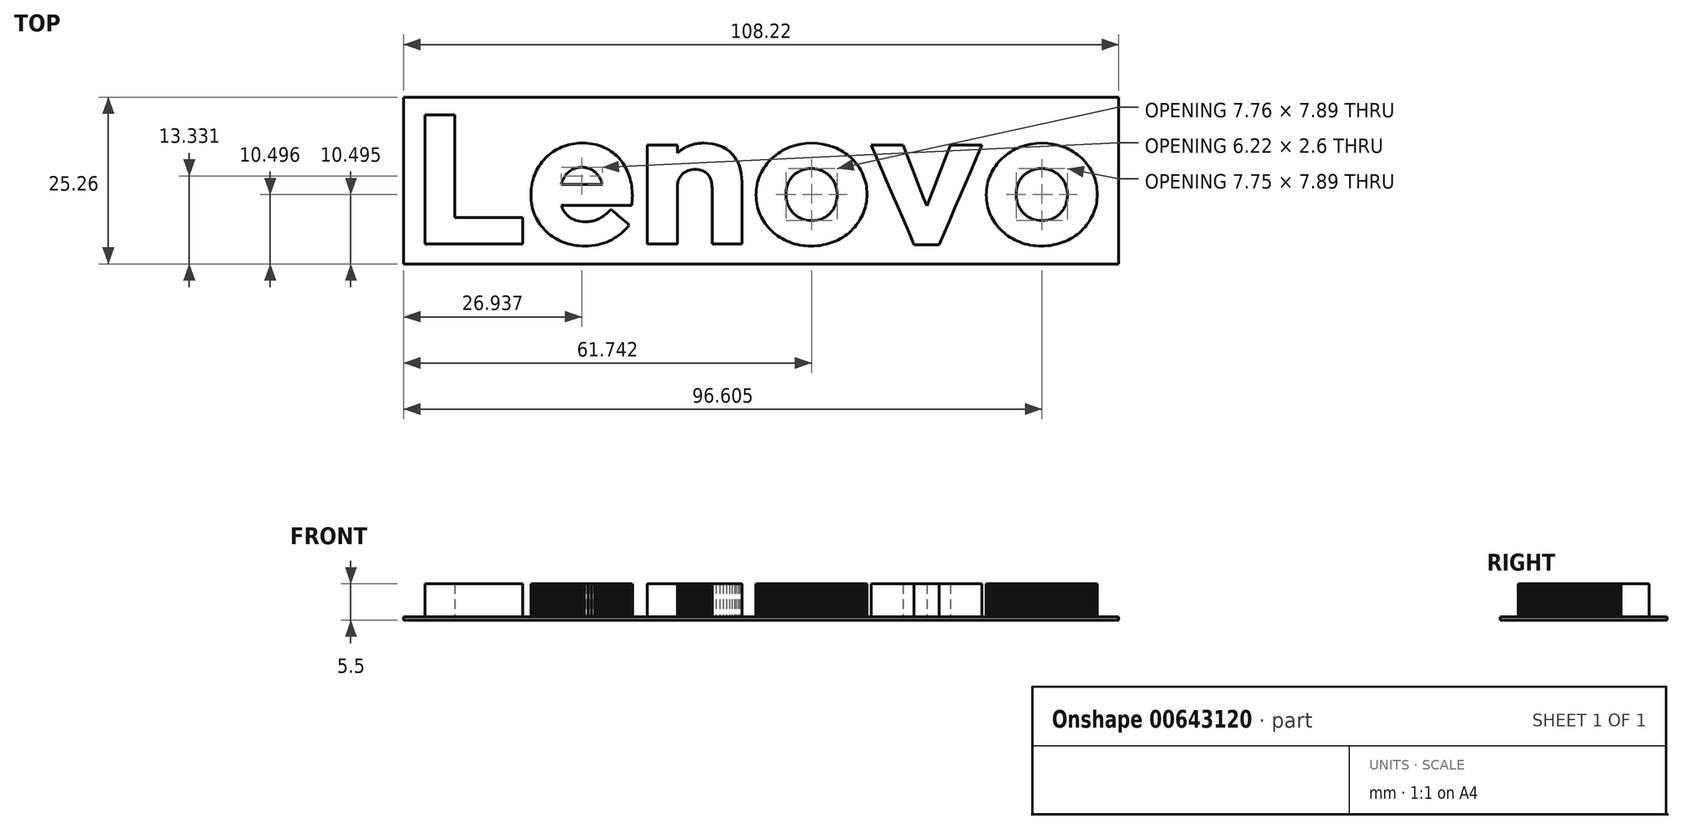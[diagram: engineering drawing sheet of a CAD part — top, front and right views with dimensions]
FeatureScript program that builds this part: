
annotation { "Feature Type Name" : "Feature", "Feature Type Description" : "" }
export const myFeature = defineFeature(function(context is Context, id is Id, definition is map)
    precondition{}
    {
        {
            var Q0;
            Q0=qCreatedBy(makeId("Top.planeOp"),FACE);
            var sketch = newSketch(context, id + "F0", { "sketchPlane" : qUnion([Q0])});
            skLineSegment(sketch, "E0", {"start": v(-46.38, -5.6) * mm, "end": v(-46.38, -3.67) * mm});
            skLineSegment(sketch, "E1", {"start": v(-46.38, -3.67) * mm, "end": v(-46.38, -1.73) * mm});
            skLineSegment(sketch, "E2", {"start": v(-46.38, -1.73) * mm, "end": v(-46.38, 0.22) * mm});
            skLineSegment(sketch, "E3", {"start": v(-46.38, 0.22) * mm, "end": v(-46.38, 2.16) * mm});
            skLineSegment(sketch, "E4", {"start": v(-46.38, 2.16) * mm, "end": v(-46.38, 4.1) * mm});
            skLineSegment(sketch, "E5", {"start": v(-46.38, 4.1) * mm, "end": v(-46.38, 6.04) * mm});
            skLineSegment(sketch, "E6", {"start": v(-46.38, 6.04) * mm, "end": v(-46.38, 7.98) * mm});
            skLineSegment(sketch, "E7", {"start": v(-46.38, 7.98) * mm, "end": v(-46.38, 9.92) * mm});
            skLineSegment(sketch, "E8", {"start": v(-46.38, 9.92) * mm, "end": v(-46.94, 9.92) * mm});
            skLineSegment(sketch, "E9", {"start": v(-46.94, 9.92) * mm, "end": v(-47.5, 9.92) * mm});
            skLineSegment(sketch, "E10", {"start": v(-47.5, 9.92) * mm, "end": v(-48.07, 9.92) * mm});
            skLineSegment(sketch, "E11", {"start": v(-48.07, 9.92) * mm, "end": v(-48.63, 9.92) * mm});
            skLineSegment(sketch, "E12", {"start": v(-48.63, 9.92) * mm, "end": v(-49.2, 9.92) * mm});
            skLineSegment(sketch, "E13", {"start": v(-49.2, 9.92) * mm, "end": v(-49.76, 9.92) * mm});
            skLineSegment(sketch, "E14", {"start": v(-49.76, 9.92) * mm, "end": v(-50.33, 9.92) * mm});
            skLineSegment(sketch, "E15", {"start": v(-50.33, 9.92) * mm, "end": v(-50.9, 9.92) * mm});
            skLineSegment(sketch, "E16", {"start": v(-50.9, 9.92) * mm, "end": v(-50.9, 7.48) * mm});
            skLineSegment(sketch, "E17", {"start": v(-50.9, 7.48) * mm, "end": v(-50.9, 5.04) * mm});
            skLineSegment(sketch, "E18", {"start": v(-50.9, 5.04) * mm, "end": v(-50.9, 2.6) * mm});
            skLineSegment(sketch, "E19", {"start": v(-50.9, 2.6) * mm, "end": v(-50.9, 0.16) * mm});
            skLineSegment(sketch, "E20", {"start": v(-50.9, 0.16) * mm, "end": v(-50.9, -2.28) * mm});
            skLineSegment(sketch, "E21", {"start": v(-50.9, -2.28) * mm, "end": v(-50.9, -4.72) * mm});
            skLineSegment(sketch, "E22", {"start": v(-50.9, -4.72) * mm, "end": v(-50.9, -7.16) * mm});
            skLineSegment(sketch, "E23", {"start": v(-50.9, -7.16) * mm, "end": v(-50.9, -9.6) * mm});
            skLineSegment(sketch, "E24", {"start": v(-50.9, -9.6) * mm, "end": v(-49.05, -9.6) * mm});
            skLineSegment(sketch, "E25", {"start": v(-49.05, -9.6) * mm, "end": v(-47.2, -9.6) * mm});
            skLineSegment(sketch, "E26", {"start": v(-47.2, -9.6) * mm, "end": v(-45.35, -9.6) * mm});
            skLineSegment(sketch, "E27", {"start": v(-45.35, -9.6) * mm, "end": v(-43.5, -9.6) * mm});
            skLineSegment(sketch, "E28", {"start": v(-43.5, -9.6) * mm, "end": v(-41.66, -9.6) * mm});
            skLineSegment(sketch, "E29", {"start": v(-41.66, -9.6) * mm, "end": v(-39.82, -9.6) * mm});
            skLineSegment(sketch, "E30", {"start": v(-39.82, -9.6) * mm, "end": v(-37.97, -9.6) * mm});
            skLineSegment(sketch, "E31", {"start": v(-37.97, -9.6) * mm, "end": v(-36.12, -9.6) * mm});
            skLineSegment(sketch, "E32", {"start": v(-36.12, -9.6) * mm, "end": v(-36.12, -9.1) * mm});
            skLineSegment(sketch, "E33", {"start": v(-36.12, -9.1) * mm, "end": v(-36.12, -8.6) * mm});
            skLineSegment(sketch, "E34", {"start": v(-36.12, -8.6) * mm, "end": v(-36.12, -8.1) * mm});
            skLineSegment(sketch, "E35", {"start": v(-36.12, -8.1) * mm, "end": v(-36.12, -7.6) * mm});
            skLineSegment(sketch, "E36", {"start": v(-36.12, -7.6) * mm, "end": v(-36.12, -7.1) * mm});
            skLineSegment(sketch, "E37", {"start": v(-36.12, -7.1) * mm, "end": v(-36.12, -6.6) * mm});
            skLineSegment(sketch, "E38", {"start": v(-36.12, -6.6) * mm, "end": v(-36.12, -6.1) * mm});
            skLineSegment(sketch, "E39", {"start": v(-36.12, -6.1) * mm, "end": v(-36.12, -5.6) * mm});
            skLineSegment(sketch, "E40", {"start": v(-36.12, -5.6) * mm, "end": v(-37.4, -5.6) * mm});
            skLineSegment(sketch, "E41", {"start": v(-37.4, -5.6) * mm, "end": v(-38.69, -5.6) * mm});
            skLineSegment(sketch, "E42", {"start": v(-38.69, -5.6) * mm, "end": v(-39.97, -5.6) * mm});
            skLineSegment(sketch, "E43", {"start": v(-39.97, -5.6) * mm, "end": v(-41.25, -5.6) * mm});
            skLineSegment(sketch, "E44", {"start": v(-41.25, -5.6) * mm, "end": v(-42.53, -5.6) * mm});
            skLineSegment(sketch, "E45", {"start": v(-42.53, -5.6) * mm, "end": v(-43.81, -5.6) * mm});
            skLineSegment(sketch, "E46", {"start": v(-43.81, -5.6) * mm, "end": v(-45.1, -5.6) * mm});
            skLineSegment(sketch, "E47", {"start": v(-45.1, -5.6) * mm, "end": v(-46.38, -5.6) * mm});
            skLineSegment(sketch, "E48", {"start": v(-24.07, -0.6) * mm, "end": v(-24.84, -0.6) * mm});
            skLineSegment(sketch, "E49", {"start": v(-24.84, -0.6) * mm, "end": v(-25.62, -0.6) * mm});
            skLineSegment(sketch, "E50", {"start": v(-25.62, -0.6) * mm, "end": v(-26.4, -0.6) * mm});
            skLineSegment(sketch, "E51", {"start": v(-26.4, -0.6) * mm, "end": v(-27.17, -0.6) * mm});
            skLineSegment(sketch, "E52", {"start": v(-27.17, -0.6) * mm, "end": v(-27.95, -0.6) * mm});
            skLineSegment(sketch, "E53", {"start": v(-27.95, -0.6) * mm, "end": v(-28.73, -0.6) * mm});
            skLineSegment(sketch, "E54", {"start": v(-28.73, -0.6) * mm, "end": v(-29.5, -0.6) * mm});
            skLineSegment(sketch, "E55", {"start": v(-29.5, -0.6) * mm, "end": v(-30.28, -0.6) * mm});
            skLineSegment(sketch, "E56", {"start": v(-30.28, -0.6) * mm, "end": v(-30.2, -0.34) * mm});
            skLineSegment(sketch, "E57", {"start": v(-30.2, -0.34) * mm, "end": v(-30.12, -0.1) * mm});
            skLineSegment(sketch, "E58", {"start": v(-30.12, -0.1) * mm, "end": v(-30.02, 0.14) * mm});
            skLineSegment(sketch, "E59", {"start": v(-30.02, 0.14) * mm, "end": v(-29.9, 0.36) * mm});
            skLineSegment(sketch, "E60", {"start": v(-29.9, 0.36) * mm, "end": v(-29.77, 0.58) * mm});
            skLineSegment(sketch, "E61", {"start": v(-29.77, 0.58) * mm, "end": v(-29.63, 0.78) * mm});
            skLineSegment(sketch, "E62", {"start": v(-29.63, 0.78) * mm, "end": v(-29.48, 0.97) * mm});
            skLineSegment(sketch, "E63", {"start": v(-29.48, 0.97) * mm, "end": v(-29.3, 1.15) * mm});
            skLineSegment(sketch, "E64", {"start": v(-29.3, 1.15) * mm, "end": v(-29.09, 1.35) * mm});
            skLineSegment(sketch, "E65", {"start": v(-29.09, 1.35) * mm, "end": v(-28.85, 1.52) * mm});
            skLineSegment(sketch, "E66", {"start": v(-28.85, 1.52) * mm, "end": v(-28.6, 1.67) * mm});
            skLineSegment(sketch, "E67", {"start": v(-28.6, 1.67) * mm, "end": v(-28.34, 1.79) * mm});
            skLineSegment(sketch, "E68", {"start": v(-28.34, 1.79) * mm, "end": v(-28.07, 1.88) * mm});
            skLineSegment(sketch, "E69", {"start": v(-28.07, 1.88) * mm, "end": v(-27.77, 1.95) * mm});
            skLineSegment(sketch, "E70", {"start": v(-27.77, 1.95) * mm, "end": v(-27.47, 1.99) * mm});
            skLineSegment(sketch, "E71", {"start": v(-27.47, 1.99) * mm, "end": v(-27.15, 2) * mm});
            skLineSegment(sketch, "E72", {"start": v(-27.15, 2) * mm, "end": v(-26.97, 2) * mm});
            skLineSegment(sketch, "E73", {"start": v(-26.97, 2) * mm, "end": v(-26.8, 1.98) * mm});
            skLineSegment(sketch, "E74", {"start": v(-26.8, 1.98) * mm, "end": v(-26.63, 1.96) * mm});
            skLineSegment(sketch, "E75", {"start": v(-26.63, 1.96) * mm, "end": v(-26.47, 1.94) * mm});
            skLineSegment(sketch, "E76", {"start": v(-26.47, 1.94) * mm, "end": v(-26.32, 1.9) * mm});
            skLineSegment(sketch, "E77", {"start": v(-26.32, 1.9) * mm, "end": v(-26.17, 1.86) * mm});
            skLineSegment(sketch, "E78", {"start": v(-26.17, 1.86) * mm, "end": v(-26.02, 1.81) * mm});
            skLineSegment(sketch, "E79", {"start": v(-26.02, 1.81) * mm, "end": v(-25.88, 1.76) * mm});
            skLineSegment(sketch, "E80", {"start": v(-25.88, 1.76) * mm, "end": v(-25.75, 1.7) * mm});
            skLineSegment(sketch, "E81", {"start": v(-25.75, 1.7) * mm, "end": v(-25.62, 1.63) * mm});
            skLineSegment(sketch, "E82", {"start": v(-25.62, 1.63) * mm, "end": v(-25.5, 1.55) * mm});
            skLineSegment(sketch, "E83", {"start": v(-25.5, 1.55) * mm, "end": v(-25.37, 1.47) * mm});
            skLineSegment(sketch, "E84", {"start": v(-25.37, 1.47) * mm, "end": v(-25.26, 1.39) * mm});
            skLineSegment(sketch, "E85", {"start": v(-25.26, 1.39) * mm, "end": v(-25.15, 1.3) * mm});
            skLineSegment(sketch, "E86", {"start": v(-25.15, 1.3) * mm, "end": v(-25.04, 1.2) * mm});
            skLineSegment(sketch, "E87", {"start": v(-25.04, 1.2) * mm, "end": v(-24.94, 1.1) * mm});
            skLineSegment(sketch, "E88", {"start": v(-24.94, 1.1) * mm, "end": v(-24.84, 1) * mm});
            skLineSegment(sketch, "E89", {"start": v(-24.84, 1) * mm, "end": v(-24.75, 0.89) * mm});
            skLineSegment(sketch, "E90", {"start": v(-24.75, 0.89) * mm, "end": v(-24.66, 0.77) * mm});
            skLineSegment(sketch, "E91", {"start": v(-24.66, 0.77) * mm, "end": v(-24.57, 0.65) * mm});
            skLineSegment(sketch, "E92", {"start": v(-24.57, 0.65) * mm, "end": v(-24.5, 0.52) * mm});
            skLineSegment(sketch, "E93", {"start": v(-24.5, 0.52) * mm, "end": v(-24.42, 0.39) * mm});
            skLineSegment(sketch, "E94", {"start": v(-24.42, 0.39) * mm, "end": v(-24.36, 0.25) * mm});
            skLineSegment(sketch, "E95", {"start": v(-24.36, 0.25) * mm, "end": v(-24.3, 0.1) * mm});
            skLineSegment(sketch, "E96", {"start": v(-24.3, 0.1) * mm, "end": v(-24.26, 0.02) * mm});
            skLineSegment(sketch, "E97", {"start": v(-24.26, 0.02) * mm, "end": v(-24.22, -0.06) * mm});
            skLineSegment(sketch, "E98", {"start": v(-24.22, -0.06) * mm, "end": v(-24.2, -0.15) * mm});
            skLineSegment(sketch, "E99", {"start": v(-24.2, -0.15) * mm, "end": v(-24.16, -0.24) * mm});
            skLineSegment(sketch, "E100", {"start": v(-24.16, -0.24) * mm, "end": v(-24.14, -0.33) * mm});
            skLineSegment(sketch, "E101", {"start": v(-24.14, -0.33) * mm, "end": v(-24.11, -0.42) * mm});
            skLineSegment(sketch, "E102", {"start": v(-24.11, -0.42) * mm, "end": v(-24.09, -0.5) * mm});
            skLineSegment(sketch, "E103", {"start": v(-24.09, -0.5) * mm, "end": v(-24.07, -0.6) * mm});
            skLineSegment(sketch, "E104", {"start": v(-19.97, 0.67) * mm, "end": v(-20.1, 1.03) * mm});
            skLineSegment(sketch, "E105", {"start": v(-20.1, 1.03) * mm, "end": v(-20.24, 1.38) * mm});
            skLineSegment(sketch, "E106", {"start": v(-20.24, 1.38) * mm, "end": v(-20.4, 1.71) * mm});
            skLineSegment(sketch, "E107", {"start": v(-20.4, 1.71) * mm, "end": v(-20.57, 2.04) * mm});
            skLineSegment(sketch, "E108", {"start": v(-20.57, 2.04) * mm, "end": v(-20.75, 2.36) * mm});
            skLineSegment(sketch, "E109", {"start": v(-20.75, 2.36) * mm, "end": v(-20.95, 2.66) * mm});
            skLineSegment(sketch, "E110", {"start": v(-20.95, 2.66) * mm, "end": v(-21.16, 2.96) * mm});
            skLineSegment(sketch, "E111", {"start": v(-21.16, 2.96) * mm, "end": v(-21.4, 3.24) * mm});
            skLineSegment(sketch, "E112", {"start": v(-21.4, 3.24) * mm, "end": v(-21.64, 3.51) * mm});
            skLineSegment(sketch, "E113", {"start": v(-21.64, 3.51) * mm, "end": v(-21.9, 3.77) * mm});
            skLineSegment(sketch, "E114", {"start": v(-21.9, 3.77) * mm, "end": v(-22.18, 4.01) * mm});
            skLineSegment(sketch, "E115", {"start": v(-22.18, 4.01) * mm, "end": v(-22.47, 4.24) * mm});
            skLineSegment(sketch, "E116", {"start": v(-22.47, 4.24) * mm, "end": v(-22.78, 4.46) * mm});
            skLineSegment(sketch, "E117", {"start": v(-22.78, 4.46) * mm, "end": v(-23.1, 4.66) * mm});
            skLineSegment(sketch, "E118", {"start": v(-23.1, 4.66) * mm, "end": v(-23.44, 4.84) * mm});
            skLineSegment(sketch, "E119", {"start": v(-23.44, 4.84) * mm, "end": v(-23.79, 5.02) * mm});
            skLineSegment(sketch, "E120", {"start": v(-23.79, 5.02) * mm, "end": v(-24.15, 5.17) * mm});
            skLineSegment(sketch, "E121", {"start": v(-24.15, 5.17) * mm, "end": v(-24.53, 5.3) * mm});
            skLineSegment(sketch, "E122", {"start": v(-24.53, 5.3) * mm, "end": v(-24.93, 5.42) * mm});
            skLineSegment(sketch, "E123", {"start": v(-24.93, 5.42) * mm, "end": v(-25.34, 5.51) * mm});
            skLineSegment(sketch, "E124", {"start": v(-25.34, 5.51) * mm, "end": v(-25.76, 5.58) * mm});
            skLineSegment(sketch, "E125", {"start": v(-25.76, 5.58) * mm, "end": v(-26.2, 5.63) * mm});
            skLineSegment(sketch, "E126", {"start": v(-26.2, 5.63) * mm, "end": v(-26.65, 5.67) * mm});
            skLineSegment(sketch, "E127", {"start": v(-26.65, 5.67) * mm, "end": v(-27.1, 5.68) * mm});
            skLineSegment(sketch, "E128", {"start": v(-27.1, 5.68) * mm, "end": v(-27.53, 5.67) * mm});
            skLineSegment(sketch, "E129", {"start": v(-27.53, 5.67) * mm, "end": v(-27.95, 5.64) * mm});
            skLineSegment(sketch, "E130", {"start": v(-27.95, 5.64) * mm, "end": v(-28.35, 5.59) * mm});
            skLineSegment(sketch, "E131", {"start": v(-28.35, 5.59) * mm, "end": v(-28.75, 5.52) * mm});
            skLineSegment(sketch, "E132", {"start": v(-28.75, 5.52) * mm, "end": v(-29.14, 5.43) * mm});
            skLineSegment(sketch, "E133", {"start": v(-29.14, 5.43) * mm, "end": v(-29.51, 5.33) * mm});
            skLineSegment(sketch, "E134", {"start": v(-29.51, 5.33) * mm, "end": v(-29.88, 5.2) * mm});
            skLineSegment(sketch, "E135", {"start": v(-29.88, 5.2) * mm, "end": v(-30.24, 5.06) * mm});
            skLineSegment(sketch, "E136", {"start": v(-30.24, 5.06) * mm, "end": v(-30.59, 4.9) * mm});
            skLineSegment(sketch, "E137", {"start": v(-30.59, 4.9) * mm, "end": v(-30.92, 4.73) * mm});
            skLineSegment(sketch, "E138", {"start": v(-30.92, 4.73) * mm, "end": v(-31.25, 4.54) * mm});
            skLineSegment(sketch, "E139", {"start": v(-31.25, 4.54) * mm, "end": v(-31.56, 4.33) * mm});
            skLineSegment(sketch, "E140", {"start": v(-31.56, 4.33) * mm, "end": v(-31.86, 4.12) * mm});
            skLineSegment(sketch, "E141", {"start": v(-31.86, 4.12) * mm, "end": v(-32.15, 3.89) * mm});
            skLineSegment(sketch, "E142", {"start": v(-32.15, 3.89) * mm, "end": v(-32.43, 3.64) * mm});
            skLineSegment(sketch, "E143", {"start": v(-32.43, 3.64) * mm, "end": v(-32.7, 3.38) * mm});
            skLineSegment(sketch, "E144", {"start": v(-32.7, 3.38) * mm, "end": v(-32.94, 3.11) * mm});
            skLineSegment(sketch, "E145", {"start": v(-32.94, 3.11) * mm, "end": v(-33.18, 2.83) * mm});
            skLineSegment(sketch, "E146", {"start": v(-33.18, 2.83) * mm, "end": v(-33.4, 2.53) * mm});
            skLineSegment(sketch, "E147", {"start": v(-33.4, 2.53) * mm, "end": v(-33.61, 2.23) * mm});
            skLineSegment(sketch, "E148", {"start": v(-33.61, 2.23) * mm, "end": v(-33.8, 1.91) * mm});
            skLineSegment(sketch, "E149", {"start": v(-33.8, 1.91) * mm, "end": v(-33.98, 1.59) * mm});
            skLineSegment(sketch, "E150", {"start": v(-33.98, 1.59) * mm, "end": v(-34.14, 1.25) * mm});
            skLineSegment(sketch, "E151", {"start": v(-34.14, 1.25) * mm, "end": v(-34.3, 0.9) * mm});
            skLineSegment(sketch, "E152", {"start": v(-34.3, 0.9) * mm, "end": v(-34.42, 0.55) * mm});
            skLineSegment(sketch, "E153", {"start": v(-34.42, 0.55) * mm, "end": v(-34.54, 0.19) * mm});
            skLineSegment(sketch, "E154", {"start": v(-34.54, 0.19) * mm, "end": v(-34.64, -0.18) * mm});
            skLineSegment(sketch, "E155", {"start": v(-34.64, -0.18) * mm, "end": v(-34.72, -0.56) * mm});
            skLineSegment(sketch, "E156", {"start": v(-34.72, -0.56) * mm, "end": v(-34.78, -0.95) * mm});
            skLineSegment(sketch, "E157", {"start": v(-34.78, -0.95) * mm, "end": v(-34.82, -1.34) * mm});
            skLineSegment(sketch, "E158", {"start": v(-34.82, -1.34) * mm, "end": v(-34.85, -1.75) * mm});
            skLineSegment(sketch, "E159", {"start": v(-34.85, -1.75) * mm, "end": v(-34.86, -2.16) * mm});
            skLineSegment(sketch, "E160", {"start": v(-34.86, -2.16) * mm, "end": v(-34.85, -2.59) * mm});
            skLineSegment(sketch, "E161", {"start": v(-34.85, -2.59) * mm, "end": v(-34.82, -3) * mm});
            skLineSegment(sketch, "E162", {"start": v(-34.82, -3) * mm, "end": v(-34.77, -3.4) * mm});
            skLineSegment(sketch, "E163", {"start": v(-34.77, -3.4) * mm, "end": v(-34.7, -3.8) * mm});
            skLineSegment(sketch, "E164", {"start": v(-34.7, -3.8) * mm, "end": v(-34.61, -4.2) * mm});
            skLineSegment(sketch, "E165", {"start": v(-34.61, -4.2) * mm, "end": v(-34.5, -4.57) * mm});
            skLineSegment(sketch, "E166", {"start": v(-34.5, -4.57) * mm, "end": v(-34.38, -4.95) * mm});
            skLineSegment(sketch, "E167", {"start": v(-34.38, -4.95) * mm, "end": v(-34.24, -5.3) * mm});
            skLineSegment(sketch, "E168", {"start": v(-34.24, -5.3) * mm, "end": v(-34.07, -5.66) * mm});
            skLineSegment(sketch, "E169", {"start": v(-34.07, -5.66) * mm, "end": v(-33.89, -6) * mm});
            skLineSegment(sketch, "E170", {"start": v(-33.89, -6) * mm, "end": v(-33.7, -6.32) * mm});
            skLineSegment(sketch, "E171", {"start": v(-33.7, -6.32) * mm, "end": v(-33.48, -6.64) * mm});
            skLineSegment(sketch, "E172", {"start": v(-33.48, -6.64) * mm, "end": v(-33.26, -6.94) * mm});
            skLineSegment(sketch, "E173", {"start": v(-33.26, -6.94) * mm, "end": v(-33.02, -7.22) * mm});
            skLineSegment(sketch, "E174", {"start": v(-33.02, -7.22) * mm, "end": v(-32.77, -7.5) * mm});
            skLineSegment(sketch, "E175", {"start": v(-32.77, -7.5) * mm, "end": v(-32.5, -7.76) * mm});
            skLineSegment(sketch, "E176", {"start": v(-32.5, -7.76) * mm, "end": v(-32.22, -8) * mm});
            skLineSegment(sketch, "E177", {"start": v(-32.22, -8) * mm, "end": v(-31.93, -8.24) * mm});
            skLineSegment(sketch, "E178", {"start": v(-31.93, -8.24) * mm, "end": v(-31.63, -8.46) * mm});
            skLineSegment(sketch, "E179", {"start": v(-31.63, -8.46) * mm, "end": v(-31.31, -8.67) * mm});
            skLineSegment(sketch, "E180", {"start": v(-31.31, -8.67) * mm, "end": v(-30.98, -8.86) * mm});
            skLineSegment(sketch, "E181", {"start": v(-30.98, -8.86) * mm, "end": v(-30.64, -9.04) * mm});
            skLineSegment(sketch, "E182", {"start": v(-30.64, -9.04) * mm, "end": v(-30.29, -9.2) * mm});
            skLineSegment(sketch, "E183", {"start": v(-30.29, -9.2) * mm, "end": v(-29.93, -9.35) * mm});
            skLineSegment(sketch, "E184", {"start": v(-29.93, -9.35) * mm, "end": v(-29.55, -9.49) * mm});
            skLineSegment(sketch, "E185", {"start": v(-29.55, -9.49) * mm, "end": v(-29.17, -9.6) * mm});
            skLineSegment(sketch, "E186", {"start": v(-29.17, -9.6) * mm, "end": v(-28.78, -9.7) * mm});
            skLineSegment(sketch, "E187", {"start": v(-28.78, -9.7) * mm, "end": v(-28.4, -9.78) * mm});
            skLineSegment(sketch, "E188", {"start": v(-28.4, -9.78) * mm, "end": v(-27.99, -9.84) * mm});
            skLineSegment(sketch, "E189", {"start": v(-27.99, -9.84) * mm, "end": v(-27.58, -9.89) * mm});
            skLineSegment(sketch, "E190", {"start": v(-27.58, -9.89) * mm, "end": v(-27.17, -9.91) * mm});
            skLineSegment(sketch, "E191", {"start": v(-27.17, -9.91) * mm, "end": v(-26.75, -9.92) * mm});
            skLineSegment(sketch, "E192", {"start": v(-26.75, -9.92) * mm, "end": v(-26.22, -9.9) * mm});
            skLineSegment(sketch, "E193", {"start": v(-26.22, -9.9) * mm, "end": v(-25.7, -9.87) * mm});
            skLineSegment(sketch, "E194", {"start": v(-25.7, -9.87) * mm, "end": v(-25.2, -9.81) * mm});
            skLineSegment(sketch, "E195", {"start": v(-25.2, -9.81) * mm, "end": v(-24.73, -9.73) * mm});
            skLineSegment(sketch, "E196", {"start": v(-24.73, -9.73) * mm, "end": v(-24.26, -9.62) * mm});
            skLineSegment(sketch, "E197", {"start": v(-24.26, -9.62) * mm, "end": v(-23.82, -9.48) * mm});
            skLineSegment(sketch, "E198", {"start": v(-23.82, -9.48) * mm, "end": v(-23.4, -9.33) * mm});
            skLineSegment(sketch, "E199", {"start": v(-23.4, -9.33) * mm, "end": v(-23, -9.15) * mm});
            skLineSegment(sketch, "E200", {"start": v(-23, -9.15) * mm, "end": v(-22.61, -8.95) * mm});
            skLineSegment(sketch, "E201", {"start": v(-22.61, -8.95) * mm, "end": v(-22.24, -8.74) * mm});
            skLineSegment(sketch, "E202", {"start": v(-22.24, -8.74) * mm, "end": v(-21.89, -8.5) * mm});
            skLineSegment(sketch, "E203", {"start": v(-21.89, -8.5) * mm, "end": v(-21.54, -8.26) * mm});
            skLineSegment(sketch, "E204", {"start": v(-21.54, -8.26) * mm, "end": v(-21.21, -8) * mm});
            skLineSegment(sketch, "E205", {"start": v(-21.21, -8) * mm, "end": v(-20.9, -7.72) * mm});
            skLineSegment(sketch, "E206", {"start": v(-20.9, -7.72) * mm, "end": v(-20.6, -7.43) * mm});
            skLineSegment(sketch, "E207", {"start": v(-20.6, -7.43) * mm, "end": v(-20.3, -7.12) * mm});
            skLineSegment(sketch, "E208", {"start": v(-20.3, -7.12) * mm, "end": v(-20.26, -7.07) * mm});
            skLineSegment(sketch, "E209", {"start": v(-20.26, -7.07) * mm, "end": v(-20.21, -7.02) * mm});
            skLineSegment(sketch, "E210", {"start": v(-20.21, -7.02) * mm, "end": v(-20.17, -6.97) * mm});
            skLineSegment(sketch, "E211", {"start": v(-20.17, -6.97) * mm, "end": v(-20.12, -6.92) * mm});
            skLineSegment(sketch, "E212", {"start": v(-20.12, -6.92) * mm, "end": v(-20.08, -6.87) * mm});
            skLineSegment(sketch, "E213", {"start": v(-20.08, -6.87) * mm, "end": v(-20.04, -6.82) * mm});
            skLineSegment(sketch, "E214", {"start": v(-20.04, -6.82) * mm, "end": v(-20, -6.77) * mm});
            skLineSegment(sketch, "E215", {"start": v(-20, -6.77) * mm, "end": v(-19.95, -6.72) * mm});
            skLineSegment(sketch, "E216", {"start": v(-19.95, -6.72) * mm, "end": v(-20.3, -6.43) * mm});
            skLineSegment(sketch, "E217", {"start": v(-20.3, -6.43) * mm, "end": v(-20.64, -6.14) * mm});
            skLineSegment(sketch, "E218", {"start": v(-20.64, -6.14) * mm, "end": v(-21, -5.85) * mm});
            skLineSegment(sketch, "E219", {"start": v(-21, -5.85) * mm, "end": v(-21.34, -5.55) * mm});
            skLineSegment(sketch, "E220", {"start": v(-21.34, -5.55) * mm, "end": v(-21.69, -5.26) * mm});
            skLineSegment(sketch, "E221", {"start": v(-21.69, -5.26) * mm, "end": v(-22.04, -4.97) * mm});
            skLineSegment(sketch, "E222", {"start": v(-22.04, -4.97) * mm, "end": v(-22.38, -4.68) * mm});
            skLineSegment(sketch, "E223", {"start": v(-22.38, -4.68) * mm, "end": v(-22.73, -4.39) * mm});
            skLineSegment(sketch, "E224", {"start": v(-22.73, -4.39) * mm, "end": v(-22.78, -4.43) * mm});
            skLineSegment(sketch, "E225", {"start": v(-22.78, -4.43) * mm, "end": v(-22.82, -4.47) * mm});
            skLineSegment(sketch, "E226", {"start": v(-22.82, -4.47) * mm, "end": v(-22.87, -4.51) * mm});
            skLineSegment(sketch, "E227", {"start": v(-22.87, -4.51) * mm, "end": v(-22.92, -4.56) * mm});
            skLineSegment(sketch, "E228", {"start": v(-22.92, -4.56) * mm, "end": v(-22.96, -4.6) * mm});
            skLineSegment(sketch, "E229", {"start": v(-22.96, -4.6) * mm, "end": v(-23.01, -4.64) * mm});
            skLineSegment(sketch, "E230", {"start": v(-23.01, -4.64) * mm, "end": v(-23.06, -4.69) * mm});
            skLineSegment(sketch, "E231", {"start": v(-23.06, -4.69) * mm, "end": v(-23.1, -4.73) * mm});
            skLineSegment(sketch, "E232", {"start": v(-23.1, -4.73) * mm, "end": v(-23.3, -4.91) * mm});
            skLineSegment(sketch, "E233", {"start": v(-23.3, -4.91) * mm, "end": v(-23.52, -5.09) * mm});
            skLineSegment(sketch, "E234", {"start": v(-23.52, -5.09) * mm, "end": v(-23.72, -5.25) * mm});
            skLineSegment(sketch, "E235", {"start": v(-23.72, -5.25) * mm, "end": v(-23.93, -5.4) * mm});
            skLineSegment(sketch, "E236", {"start": v(-23.93, -5.4) * mm, "end": v(-24.14, -5.53) * mm});
            skLineSegment(sketch, "E237", {"start": v(-24.14, -5.53) * mm, "end": v(-24.35, -5.66) * mm});
            skLineSegment(sketch, "E238", {"start": v(-24.35, -5.66) * mm, "end": v(-24.55, -5.77) * mm});
            skLineSegment(sketch, "E239", {"start": v(-24.55, -5.77) * mm, "end": v(-24.76, -5.87) * mm});
            skLineSegment(sketch, "E240", {"start": v(-24.76, -5.87) * mm, "end": v(-24.97, -5.96) * mm});
            skLineSegment(sketch, "E241", {"start": v(-24.97, -5.96) * mm, "end": v(-25.18, -6.03) * mm});
            skLineSegment(sketch, "E242", {"start": v(-25.18, -6.03) * mm, "end": v(-25.41, -6.1) * mm});
            skLineSegment(sketch, "E243", {"start": v(-25.41, -6.1) * mm, "end": v(-25.65, -6.15) * mm});
            skLineSegment(sketch, "E244", {"start": v(-25.65, -6.15) * mm, "end": v(-25.9, -6.19) * mm});
            skLineSegment(sketch, "E245", {"start": v(-25.9, -6.19) * mm, "end": v(-26.15, -6.22) * mm});
            skLineSegment(sketch, "E246", {"start": v(-26.15, -6.22) * mm, "end": v(-26.42, -6.23) * mm});
            skLineSegment(sketch, "E247", {"start": v(-26.42, -6.23) * mm, "end": v(-26.69, -6.24) * mm});
            skLineSegment(sketch, "E248", {"start": v(-26.69, -6.24) * mm, "end": v(-27.04, -6.23) * mm});
            skLineSegment(sketch, "E249", {"start": v(-27.04, -6.23) * mm, "end": v(-27.39, -6.2) * mm});
            skLineSegment(sketch, "E250", {"start": v(-27.39, -6.2) * mm, "end": v(-27.71, -6.13) * mm});
            skLineSegment(sketch, "E251", {"start": v(-27.71, -6.13) * mm, "end": v(-28.02, -6.04) * mm});
            skLineSegment(sketch, "E252", {"start": v(-28.02, -6.04) * mm, "end": v(-28.32, -5.94) * mm});
            skLineSegment(sketch, "E253", {"start": v(-28.32, -5.94) * mm, "end": v(-28.6, -5.8) * mm});
            skLineSegment(sketch, "E254", {"start": v(-28.6, -5.8) * mm, "end": v(-28.87, -5.64) * mm});
            skLineSegment(sketch, "E255", {"start": v(-28.87, -5.64) * mm, "end": v(-29.13, -5.46) * mm});
            skLineSegment(sketch, "E256", {"start": v(-29.13, -5.46) * mm, "end": v(-29.32, -5.3) * mm});
            skLineSegment(sketch, "E257", {"start": v(-29.32, -5.3) * mm, "end": v(-29.5, -5.12) * mm});
            skLineSegment(sketch, "E258", {"start": v(-29.5, -5.12) * mm, "end": v(-29.65, -4.93) * mm});
            skLineSegment(sketch, "E259", {"start": v(-29.65, -4.93) * mm, "end": v(-29.8, -4.73) * mm});
            skLineSegment(sketch, "E260", {"start": v(-29.8, -4.73) * mm, "end": v(-29.93, -4.51) * mm});
            skLineSegment(sketch, "E261", {"start": v(-29.93, -4.51) * mm, "end": v(-30.04, -4.28) * mm});
            skLineSegment(sketch, "E262", {"start": v(-30.04, -4.28) * mm, "end": v(-30.15, -4.04) * mm});
            skLineSegment(sketch, "E263", {"start": v(-30.15, -4.04) * mm, "end": v(-30.23, -3.78) * mm});
            skLineSegment(sketch, "E264", {"start": v(-30.23, -3.78) * mm, "end": v(-28.9, -3.78) * mm});
            skLineSegment(sketch, "E265", {"start": v(-28.9, -3.78) * mm, "end": v(-27.58, -3.78) * mm});
            skLineSegment(sketch, "E266", {"start": v(-27.58, -3.78) * mm, "end": v(-26.25, -3.78) * mm});
            skLineSegment(sketch, "E267", {"start": v(-26.25, -3.78) * mm, "end": v(-24.93, -3.78) * mm});
            skLineSegment(sketch, "E268", {"start": v(-24.93, -3.78) * mm, "end": v(-23.6, -3.78) * mm});
            skLineSegment(sketch, "E269", {"start": v(-23.6, -3.78) * mm, "end": v(-22.27, -3.78) * mm});
            skLineSegment(sketch, "E270", {"start": v(-22.27, -3.78) * mm, "end": v(-20.94, -3.78) * mm});
            skLineSegment(sketch, "E271", {"start": v(-20.94, -3.78) * mm, "end": v(-19.62, -3.78) * mm});
            skLineSegment(sketch, "E272", {"start": v(-19.62, -3.78) * mm, "end": v(-19.61, -3.72) * mm});
            skLineSegment(sketch, "E273", {"start": v(-19.61, -3.72) * mm, "end": v(-19.6, -3.66) * mm});
            skLineSegment(sketch, "E274", {"start": v(-19.6, -3.66) * mm, "end": v(-19.6, -3.6) * mm});
            skLineSegment(sketch, "E275", {"start": v(-19.6, -3.6) * mm, "end": v(-19.59, -3.54) * mm});
            skLineSegment(sketch, "E276", {"start": v(-19.59, -3.54) * mm, "end": v(-19.58, -3.48) * mm});
            skLineSegment(sketch, "E277", {"start": v(-19.58, -3.48) * mm, "end": v(-19.58, -3.42) * mm});
            skLineSegment(sketch, "E278", {"start": v(-19.58, -3.42) * mm, "end": v(-19.57, -3.36) * mm});
            skLineSegment(sketch, "E279", {"start": v(-19.57, -3.36) * mm, "end": v(-19.56, -3.3) * mm});
            skLineSegment(sketch, "E280", {"start": v(-19.56, -3.3) * mm, "end": v(-19.55, -3.24) * mm});
            skLineSegment(sketch, "E281", {"start": v(-19.55, -3.24) * mm, "end": v(-19.55, -3.18) * mm});
            skLineSegment(sketch, "E282", {"start": v(-19.55, -3.18) * mm, "end": v(-19.54, -3.11) * mm});
            skLineSegment(sketch, "E283", {"start": v(-19.54, -3.11) * mm, "end": v(-19.53, -3.05) * mm});
            skLineSegment(sketch, "E284", {"start": v(-19.53, -3.05) * mm, "end": v(-19.53, -3) * mm});
            skLineSegment(sketch, "E285", {"start": v(-19.53, -3) * mm, "end": v(-19.52, -2.93) * mm});
            skLineSegment(sketch, "E286", {"start": v(-19.52, -2.93) * mm, "end": v(-19.52, -2.87) * mm});
            skLineSegment(sketch, "E287", {"start": v(-19.52, -2.87) * mm, "end": v(-19.52, -2.81) * mm});
            skLineSegment(sketch, "E288", {"start": v(-19.52, -2.81) * mm, "end": v(-19.51, -2.75) * mm});
            skLineSegment(sketch, "E289", {"start": v(-19.51, -2.75) * mm, "end": v(-19.51, -2.7) * mm});
            skLineSegment(sketch, "E290", {"start": v(-19.51, -2.7) * mm, "end": v(-19.5, -2.63) * mm});
            skLineSegment(sketch, "E291", {"start": v(-19.5, -2.63) * mm, "end": v(-19.5, -2.58) * mm});
            skLineSegment(sketch, "E292", {"start": v(-19.5, -2.58) * mm, "end": v(-19.5, -2.52) * mm});
            skLineSegment(sketch, "E293", {"start": v(-19.5, -2.52) * mm, "end": v(-19.5, -2.46) * mm});
            skLineSegment(sketch, "E294", {"start": v(-19.5, -2.46) * mm, "end": v(-19.5, -2.4) * mm});
            skLineSegment(sketch, "E295", {"start": v(-19.5, -2.4) * mm, "end": v(-19.5, -2.35) * mm});
            skLineSegment(sketch, "E296", {"start": v(-19.5, -2.35) * mm, "end": v(-19.5, -1.95) * mm});
            skLineSegment(sketch, "E297", {"start": v(-19.5, -1.95) * mm, "end": v(-19.53, -1.57) * mm});
            skLineSegment(sketch, "E298", {"start": v(-19.53, -1.57) * mm, "end": v(-19.57, -1.18) * mm});
            skLineSegment(sketch, "E299", {"start": v(-19.57, -1.18) * mm, "end": v(-19.62, -0.8) * mm});
            skLineSegment(sketch, "E300", {"start": v(-19.62, -0.8) * mm, "end": v(-19.69, -0.42) * mm});
            skLineSegment(sketch, "E301", {"start": v(-19.69, -0.42) * mm, "end": v(-19.77, -0.05) * mm});
            skLineSegment(sketch, "E302", {"start": v(-19.77, -0.05) * mm, "end": v(-19.86, 0.31) * mm});
            skLineSegment(sketch, "E303", {"start": v(-19.86, 0.31) * mm, "end": v(-19.97, 0.67) * mm});
            skLineSegment(sketch, "E304", {"start": v(-4.4, 4.05) * mm, "end": v(-4.8, 4.43) * mm});
            skLineSegment(sketch, "E305", {"start": v(-4.8, 4.43) * mm, "end": v(-5.25, 4.76) * mm});
            skLineSegment(sketch, "E306", {"start": v(-5.25, 4.76) * mm, "end": v(-5.73, 5.04) * mm});
            skLineSegment(sketch, "E307", {"start": v(-5.73, 5.04) * mm, "end": v(-6.25, 5.27) * mm});
            skLineSegment(sketch, "E308", {"start": v(-6.25, 5.27) * mm, "end": v(-6.8, 5.45) * mm});
            skLineSegment(sketch, "E309", {"start": v(-6.8, 5.45) * mm, "end": v(-7.4, 5.57) * mm});
            skLineSegment(sketch, "E310", {"start": v(-7.4, 5.57) * mm, "end": v(-8.02, 5.65) * mm});
            skLineSegment(sketch, "E311", {"start": v(-8.02, 5.65) * mm, "end": v(-8.69, 5.68) * mm});
            skLineSegment(sketch, "E312", {"start": v(-8.69, 5.68) * mm, "end": v(-8.92, 5.67) * mm});
            skLineSegment(sketch, "E313", {"start": v(-8.92, 5.67) * mm, "end": v(-9.15, 5.66) * mm});
            skLineSegment(sketch, "E314", {"start": v(-9.15, 5.66) * mm, "end": v(-9.37, 5.64) * mm});
            skLineSegment(sketch, "E315", {"start": v(-9.37, 5.64) * mm, "end": v(-9.59, 5.62) * mm});
            skLineSegment(sketch, "E316", {"start": v(-9.59, 5.62) * mm, "end": v(-9.8, 5.59) * mm});
            skLineSegment(sketch, "E317", {"start": v(-9.8, 5.59) * mm, "end": v(-10, 5.55) * mm});
            skLineSegment(sketch, "E318", {"start": v(-10, 5.55) * mm, "end": v(-10.2, 5.5) * mm});
            skLineSegment(sketch, "E319", {"start": v(-10.2, 5.5) * mm, "end": v(-10.4, 5.45) * mm});
            skLineSegment(sketch, "E320", {"start": v(-10.4, 5.45) * mm, "end": v(-10.58, 5.4) * mm});
            skLineSegment(sketch, "E321", {"start": v(-10.58, 5.4) * mm, "end": v(-10.76, 5.33) * mm});
            skLineSegment(sketch, "E322", {"start": v(-10.76, 5.33) * mm, "end": v(-10.94, 5.27) * mm});
            skLineSegment(sketch, "E323", {"start": v(-10.94, 5.27) * mm, "end": v(-11.12, 5.2) * mm});
            skLineSegment(sketch, "E324", {"start": v(-11.12, 5.2) * mm, "end": v(-11.3, 5.11) * mm});
            skLineSegment(sketch, "E325", {"start": v(-11.3, 5.11) * mm, "end": v(-11.46, 5.03) * mm});
            skLineSegment(sketch, "E326", {"start": v(-11.46, 5.03) * mm, "end": v(-11.63, 4.94) * mm});
            skLineSegment(sketch, "E327", {"start": v(-11.63, 4.94) * mm, "end": v(-11.79, 4.85) * mm});
            skLineSegment(sketch, "E328", {"start": v(-11.79, 4.85) * mm, "end": v(-11.91, 4.77) * mm});
            skLineSegment(sketch, "E329", {"start": v(-11.91, 4.77) * mm, "end": v(-12.03, 4.69) * mm});
            skLineSegment(sketch, "E330", {"start": v(-12.03, 4.69) * mm, "end": v(-12.15, 4.6) * mm});
            skLineSegment(sketch, "E331", {"start": v(-12.15, 4.6) * mm, "end": v(-12.27, 4.52) * mm});
            skLineSegment(sketch, "E332", {"start": v(-12.27, 4.52) * mm, "end": v(-12.38, 4.43) * mm});
            skLineSegment(sketch, "E333", {"start": v(-12.38, 4.43) * mm, "end": v(-12.5, 4.34) * mm});
            skLineSegment(sketch, "E334", {"start": v(-12.5, 4.34) * mm, "end": v(-12.6, 4.25) * mm});
            skLineSegment(sketch, "E335", {"start": v(-12.6, 4.25) * mm, "end": v(-12.7, 4.16) * mm});
            skLineSegment(sketch, "E336", {"start": v(-12.7, 4.16) * mm, "end": v(-12.7, 4.3) * mm});
            skLineSegment(sketch, "E337", {"start": v(-12.7, 4.3) * mm, "end": v(-12.7, 4.46) * mm});
            skLineSegment(sketch, "E338", {"start": v(-12.7, 4.46) * mm, "end": v(-12.7, 4.62) * mm});
            skLineSegment(sketch, "E339", {"start": v(-12.7, 4.62) * mm, "end": v(-12.7, 4.77) * mm});
            skLineSegment(sketch, "E340", {"start": v(-12.7, 4.77) * mm, "end": v(-12.7, 4.93) * mm});
            skLineSegment(sketch, "E341", {"start": v(-12.7, 4.93) * mm, "end": v(-12.7, 5.08) * mm});
            skLineSegment(sketch, "E342", {"start": v(-12.7, 5.08) * mm, "end": v(-12.7, 5.23) * mm});
            skLineSegment(sketch, "E343", {"start": v(-12.7, 5.23) * mm, "end": v(-12.7, 5.39) * mm});
            skLineSegment(sketch, "E344", {"start": v(-12.7, 5.39) * mm, "end": v(-13.27, 5.39) * mm});
            skLineSegment(sketch, "E345", {"start": v(-13.27, 5.39) * mm, "end": v(-13.84, 5.39) * mm});
            skLineSegment(sketch, "E346", {"start": v(-13.84, 5.39) * mm, "end": v(-14.4, 5.39) * mm});
            skLineSegment(sketch, "E347", {"start": v(-14.4, 5.39) * mm, "end": v(-14.97, 5.39) * mm});
            skLineSegment(sketch, "E348", {"start": v(-14.97, 5.39) * mm, "end": v(-15.53, 5.39) * mm});
            skLineSegment(sketch, "E349", {"start": v(-15.53, 5.39) * mm, "end": v(-16.1, 5.39) * mm});
            skLineSegment(sketch, "E350", {"start": v(-16.1, 5.39) * mm, "end": v(-16.67, 5.39) * mm});
            skLineSegment(sketch, "E351", {"start": v(-16.67, 5.39) * mm, "end": v(-17.23, 5.39) * mm});
            skLineSegment(sketch, "E352", {"start": v(-17.23, 5.39) * mm, "end": v(-17.23, 3.51) * mm});
            skLineSegment(sketch, "E353", {"start": v(-17.23, 3.51) * mm, "end": v(-17.23, 1.64) * mm});
            skLineSegment(sketch, "E354", {"start": v(-17.23, 1.64) * mm, "end": v(-17.23, -0.23) * mm});
            skLineSegment(sketch, "E355", {"start": v(-17.23, -0.23) * mm, "end": v(-17.23, -2.1) * mm});
            skLineSegment(sketch, "E356", {"start": v(-17.23, -2.1) * mm, "end": v(-17.23, -3.98) * mm});
            skLineSegment(sketch, "E357", {"start": v(-17.23, -3.98) * mm, "end": v(-17.23, -5.85) * mm});
            skLineSegment(sketch, "E358", {"start": v(-17.23, -5.85) * mm, "end": v(-17.23, -7.73) * mm});
            skLineSegment(sketch, "E359", {"start": v(-17.23, -7.73) * mm, "end": v(-17.23, -9.6) * mm});
            skLineSegment(sketch, "E360", {"start": v(-17.23, -9.6) * mm, "end": v(-16.67, -9.6) * mm});
            skLineSegment(sketch, "E361", {"start": v(-16.67, -9.6) * mm, "end": v(-16.1, -9.6) * mm});
            skLineSegment(sketch, "E362", {"start": v(-16.1, -9.6) * mm, "end": v(-15.53, -9.6) * mm});
            skLineSegment(sketch, "E363", {"start": v(-15.53, -9.6) * mm, "end": v(-14.97, -9.6) * mm});
            skLineSegment(sketch, "E364", {"start": v(-14.97, -9.6) * mm, "end": v(-14.4, -9.6) * mm});
            skLineSegment(sketch, "E365", {"start": v(-14.4, -9.6) * mm, "end": v(-13.84, -9.6) * mm});
            skLineSegment(sketch, "E366", {"start": v(-13.84, -9.6) * mm, "end": v(-13.27, -9.6) * mm});
            skLineSegment(sketch, "E367", {"start": v(-13.27, -9.6) * mm, "end": v(-12.7, -9.6) * mm});
            skLineSegment(sketch, "E368", {"start": v(-12.7, -9.6) * mm, "end": v(-12.7, -8.56) * mm});
            skLineSegment(sketch, "E369", {"start": v(-12.7, -8.56) * mm, "end": v(-12.7, -7.5) * mm});
            skLineSegment(sketch, "E370", {"start": v(-12.7, -7.5) * mm, "end": v(-12.7, -6.46) * mm});
            skLineSegment(sketch, "E371", {"start": v(-12.7, -6.46) * mm, "end": v(-12.7, -5.42) * mm});
            skLineSegment(sketch, "E372", {"start": v(-12.7, -5.42) * mm, "end": v(-12.7, -4.37) * mm});
            skLineSegment(sketch, "E373", {"start": v(-12.7, -4.37) * mm, "end": v(-12.7, -3.32) * mm});
            skLineSegment(sketch, "E374", {"start": v(-12.7, -3.32) * mm, "end": v(-12.7, -2.28) * mm});
            skLineSegment(sketch, "E375", {"start": v(-12.7, -2.28) * mm, "end": v(-12.7, -1.23) * mm});
            skLineSegment(sketch, "E376", {"start": v(-12.7, -1.23) * mm, "end": v(-12.7, -0.88) * mm});
            skLineSegment(sketch, "E377", {"start": v(-12.7, -0.88) * mm, "end": v(-12.66, -0.56) * mm});
            skLineSegment(sketch, "E378", {"start": v(-12.66, -0.56) * mm, "end": v(-12.6, -0.26) * mm});
            skLineSegment(sketch, "E379", {"start": v(-12.6, -0.26) * mm, "end": v(-12.52, 0.02) * mm});
            skLineSegment(sketch, "E380", {"start": v(-12.52, 0.02) * mm, "end": v(-12.41, 0.28) * mm});
            skLineSegment(sketch, "E381", {"start": v(-12.41, 0.28) * mm, "end": v(-12.28, 0.52) * mm});
            skLineSegment(sketch, "E382", {"start": v(-12.28, 0.52) * mm, "end": v(-12.13, 0.74) * mm});
            skLineSegment(sketch, "E383", {"start": v(-12.13, 0.74) * mm, "end": v(-11.95, 0.94) * mm});
            skLineSegment(sketch, "E384", {"start": v(-11.95, 0.94) * mm, "end": v(-11.76, 1.11) * mm});
            skLineSegment(sketch, "E385", {"start": v(-11.76, 1.11) * mm, "end": v(-11.55, 1.27) * mm});
            skLineSegment(sketch, "E386", {"start": v(-11.55, 1.27) * mm, "end": v(-11.33, 1.4) * mm});
            skLineSegment(sketch, "E387", {"start": v(-11.33, 1.4) * mm, "end": v(-11.09, 1.5) * mm});
            skLineSegment(sketch, "E388", {"start": v(-11.09, 1.5) * mm, "end": v(-10.84, 1.58) * mm});
            skLineSegment(sketch, "E389", {"start": v(-10.84, 1.58) * mm, "end": v(-10.57, 1.64) * mm});
            skLineSegment(sketch, "E390", {"start": v(-10.57, 1.64) * mm, "end": v(-10.28, 1.67) * mm});
            skLineSegment(sketch, "E391", {"start": v(-10.28, 1.67) * mm, "end": v(-9.98, 1.68) * mm});
            skLineSegment(sketch, "E392", {"start": v(-9.98, 1.68) * mm, "end": v(-9.68, 1.67) * mm});
            skLineSegment(sketch, "E393", {"start": v(-9.68, 1.67) * mm, "end": v(-9.4, 1.64) * mm});
            skLineSegment(sketch, "E394", {"start": v(-9.4, 1.64) * mm, "end": v(-9.14, 1.58) * mm});
            skLineSegment(sketch, "E395", {"start": v(-9.14, 1.58) * mm, "end": v(-8.9, 1.5) * mm});
            skLineSegment(sketch, "E396", {"start": v(-8.9, 1.5) * mm, "end": v(-8.67, 1.41) * mm});
            skLineSegment(sketch, "E397", {"start": v(-8.67, 1.41) * mm, "end": v(-8.46, 1.3) * mm});
            skLineSegment(sketch, "E398", {"start": v(-8.46, 1.3) * mm, "end": v(-8.27, 1.15) * mm});
            skLineSegment(sketch, "E399", {"start": v(-8.27, 1.15) * mm, "end": v(-8.1, 0.99) * mm});
            skLineSegment(sketch, "E400", {"start": v(-8.1, 0.99) * mm, "end": v(-7.94, 0.8) * mm});
            skLineSegment(sketch, "E401", {"start": v(-7.94, 0.8) * mm, "end": v(-7.8, 0.58) * mm});
            skLineSegment(sketch, "E402", {"start": v(-7.8, 0.58) * mm, "end": v(-7.7, 0.34) * mm});
            skLineSegment(sketch, "E403", {"start": v(-7.7, 0.34) * mm, "end": v(-7.6, 0.08) * mm});
            skLineSegment(sketch, "E404", {"start": v(-7.6, 0.08) * mm, "end": v(-7.52, -0.2) * mm});
            skLineSegment(sketch, "E405", {"start": v(-7.52, -0.2) * mm, "end": v(-7.47, -0.5) * mm});
            skLineSegment(sketch, "E406", {"start": v(-7.47, -0.5) * mm, "end": v(-7.44, -0.83) * mm});
            skLineSegment(sketch, "E407", {"start": v(-7.44, -0.83) * mm, "end": v(-7.43, -1.18) * mm});
            skLineSegment(sketch, "E408", {"start": v(-7.43, -1.18) * mm, "end": v(-7.43, -2.23) * mm});
            skLineSegment(sketch, "E409", {"start": v(-7.43, -2.23) * mm, "end": v(-7.43, -3.28) * mm});
            skLineSegment(sketch, "E410", {"start": v(-7.43, -3.28) * mm, "end": v(-7.43, -4.34) * mm});
            skLineSegment(sketch, "E411", {"start": v(-7.43, -4.34) * mm, "end": v(-7.43, -5.39) * mm});
            skLineSegment(sketch, "E412", {"start": v(-7.43, -5.39) * mm, "end": v(-7.43, -6.44) * mm});
            skLineSegment(sketch, "E413", {"start": v(-7.43, -6.44) * mm, "end": v(-7.43, -7.5) * mm});
            skLineSegment(sketch, "E414", {"start": v(-7.43, -7.5) * mm, "end": v(-7.43, -8.55) * mm});
            skLineSegment(sketch, "E415", {"start": v(-7.43, -8.55) * mm, "end": v(-7.43, -9.6) * mm});
            skLineSegment(sketch, "E416", {"start": v(-7.43, -9.6) * mm, "end": v(-6.86, -9.6) * mm});
            skLineSegment(sketch, "E417", {"start": v(-6.86, -9.6) * mm, "end": v(-6.3, -9.6) * mm});
            skLineSegment(sketch, "E418", {"start": v(-6.3, -9.6) * mm, "end": v(-5.73, -9.6) * mm});
            skLineSegment(sketch, "E419", {"start": v(-5.73, -9.6) * mm, "end": v(-5.17, -9.6) * mm});
            skLineSegment(sketch, "E420", {"start": v(-5.17, -9.6) * mm, "end": v(-4.6, -9.6) * mm});
            skLineSegment(sketch, "E421", {"start": v(-4.6, -9.6) * mm, "end": v(-4.04, -9.6) * mm});
            skLineSegment(sketch, "E422", {"start": v(-4.04, -9.6) * mm, "end": v(-3.47, -9.6) * mm});
            skLineSegment(sketch, "E423", {"start": v(-3.47, -9.6) * mm, "end": v(-2.9, -9.6) * mm});
            skLineSegment(sketch, "E424", {"start": v(-2.9, -9.6) * mm, "end": v(-2.9, -8.43) * mm});
            skLineSegment(sketch, "E425", {"start": v(-2.9, -8.43) * mm, "end": v(-2.9, -7.25) * mm});
            skLineSegment(sketch, "E426", {"start": v(-2.9, -7.25) * mm, "end": v(-2.9, -6.08) * mm});
            skLineSegment(sketch, "E427", {"start": v(-2.9, -6.08) * mm, "end": v(-2.9, -4.9) * mm});
            skLineSegment(sketch, "E428", {"start": v(-2.9, -4.9) * mm, "end": v(-2.9, -3.73) * mm});
            skLineSegment(sketch, "E429", {"start": v(-2.9, -3.73) * mm, "end": v(-2.9, -2.56) * mm});
            skLineSegment(sketch, "E430", {"start": v(-2.9, -2.56) * mm, "end": v(-2.9, -1.38) * mm});
            skLineSegment(sketch, "E431", {"start": v(-2.9, -1.38) * mm, "end": v(-2.9, -0.2) * mm});
            skLineSegment(sketch, "E432", {"start": v(-2.9, -0.2) * mm, "end": v(-2.93, 0.44) * mm});
            skLineSegment(sketch, "E433", {"start": v(-2.93, 0.44) * mm, "end": v(-3, 1.05) * mm});
            skLineSegment(sketch, "E434", {"start": v(-3, 1.05) * mm, "end": v(-3.12, 1.63) * mm});
            skLineSegment(sketch, "E435", {"start": v(-3.12, 1.63) * mm, "end": v(-3.28, 2.18) * mm});
            skLineSegment(sketch, "E436", {"start": v(-3.28, 2.18) * mm, "end": v(-3.5, 2.7) * mm});
            skLineSegment(sketch, "E437", {"start": v(-3.5, 2.7) * mm, "end": v(-3.75, 3.18) * mm});
            skLineSegment(sketch, "E438", {"start": v(-3.75, 3.18) * mm, "end": v(-4.06, 3.63) * mm});
            skLineSegment(sketch, "E439", {"start": v(-4.06, 3.63) * mm, "end": v(-4.4, 4.05) * mm});
            skLineSegment(sketch, "E440", {"start": v(6.1, -5.78) * mm, "end": v(5.92, -5.7) * mm});
            skLineSegment(sketch, "E441", {"start": v(5.92, -5.7) * mm, "end": v(5.75, -5.6) * mm});
            skLineSegment(sketch, "E442", {"start": v(5.75, -5.6) * mm, "end": v(5.59, -5.51) * mm});
            skLineSegment(sketch, "E443", {"start": v(5.59, -5.51) * mm, "end": v(5.43, -5.4) * mm});
            skLineSegment(sketch, "E444", {"start": v(5.43, -5.4) * mm, "end": v(5.28, -5.3) * mm});
            skLineSegment(sketch, "E445", {"start": v(5.28, -5.3) * mm, "end": v(5.13, -5.18) * mm});
            skLineSegment(sketch, "E446", {"start": v(5.13, -5.18) * mm, "end": v(5, -5.06) * mm});
            skLineSegment(sketch, "E447", {"start": v(5, -5.06) * mm, "end": v(4.86, -4.93) * mm});
            skLineSegment(sketch, "E448", {"start": v(4.86, -4.93) * mm, "end": v(4.74, -4.79) * mm});
            skLineSegment(sketch, "E449", {"start": v(4.74, -4.79) * mm, "end": v(4.62, -4.64) * mm});
            skLineSegment(sketch, "E450", {"start": v(4.62, -4.64) * mm, "end": v(4.5, -4.5) * mm});
            skLineSegment(sketch, "E451", {"start": v(4.5, -4.5) * mm, "end": v(4.4, -4.34) * mm});
            skLineSegment(sketch, "E452", {"start": v(4.4, -4.34) * mm, "end": v(4.3, -4.18) * mm});
            skLineSegment(sketch, "E453", {"start": v(4.3, -4.18) * mm, "end": v(4.2, -4.01) * mm});
            skLineSegment(sketch, "E454", {"start": v(4.2, -4.01) * mm, "end": v(4.12, -3.84) * mm});
            skLineSegment(sketch, "E455", {"start": v(4.12, -3.84) * mm, "end": v(4.05, -3.67) * mm});
            skLineSegment(sketch, "E456", {"start": v(4.05, -3.67) * mm, "end": v(3.98, -3.49) * mm});
            skLineSegment(sketch, "E457", {"start": v(3.98, -3.49) * mm, "end": v(3.92, -3.3) * mm});
            skLineSegment(sketch, "E458", {"start": v(3.92, -3.3) * mm, "end": v(3.87, -3.12) * mm});
            skLineSegment(sketch, "E459", {"start": v(3.87, -3.12) * mm, "end": v(3.83, -2.92) * mm});
            skLineSegment(sketch, "E460", {"start": v(3.83, -2.92) * mm, "end": v(3.8, -2.72) * mm});
            skLineSegment(sketch, "E461", {"start": v(3.8, -2.72) * mm, "end": v(3.77, -2.52) * mm});
            skLineSegment(sketch, "E462", {"start": v(3.77, -2.52) * mm, "end": v(3.76, -2.3) * mm});
            skLineSegment(sketch, "E463", {"start": v(3.76, -2.3) * mm, "end": v(3.75, -2.08) * mm});
            skLineSegment(sketch, "E464", {"start": v(3.75, -2.08) * mm, "end": v(3.76, -1.88) * mm});
            skLineSegment(sketch, "E465", {"start": v(3.76, -1.88) * mm, "end": v(3.77, -1.68) * mm});
            skLineSegment(sketch, "E466", {"start": v(3.77, -1.68) * mm, "end": v(3.79, -1.49) * mm});
            skLineSegment(sketch, "E467", {"start": v(3.79, -1.49) * mm, "end": v(3.82, -1.3) * mm});
            skLineSegment(sketch, "E468", {"start": v(3.82, -1.3) * mm, "end": v(3.86, -1.1) * mm});
            skLineSegment(sketch, "E469", {"start": v(3.86, -1.1) * mm, "end": v(3.9, -0.92) * mm});
            skLineSegment(sketch, "E470", {"start": v(3.9, -0.92) * mm, "end": v(3.96, -0.73) * mm});
            skLineSegment(sketch, "E471", {"start": v(3.96, -0.73) * mm, "end": v(4.02, -0.55) * mm});
            skLineSegment(sketch, "E472", {"start": v(4.02, -0.55) * mm, "end": v(4.09, -0.37) * mm});
            skLineSegment(sketch, "E473", {"start": v(4.09, -0.37) * mm, "end": v(4.17, -0.2) * mm});
            skLineSegment(sketch, "E474", {"start": v(4.17, -0.2) * mm, "end": v(4.25, -0.04) * mm});
            skLineSegment(sketch, "E475", {"start": v(4.25, -0.04) * mm, "end": v(4.35, 0.11) * mm});
            skLineSegment(sketch, "E476", {"start": v(4.35, 0.11) * mm, "end": v(4.45, 0.26) * mm});
            skLineSegment(sketch, "E477", {"start": v(4.45, 0.26) * mm, "end": v(4.56, 0.4) * mm});
            skLineSegment(sketch, "E478", {"start": v(4.56, 0.4) * mm, "end": v(4.67, 0.55) * mm});
            skLineSegment(sketch, "E479", {"start": v(4.67, 0.55) * mm, "end": v(4.8, 0.68) * mm});
            skLineSegment(sketch, "E480", {"start": v(4.8, 0.68) * mm, "end": v(4.92, 0.8) * mm});
            skLineSegment(sketch, "E481", {"start": v(4.92, 0.8) * mm, "end": v(5.06, 0.92) * mm});
            skLineSegment(sketch, "E482", {"start": v(5.06, 0.92) * mm, "end": v(5.2, 1.04) * mm});
            skLineSegment(sketch, "E483", {"start": v(5.2, 1.04) * mm, "end": v(5.35, 1.14) * mm});
            skLineSegment(sketch, "E484", {"start": v(5.35, 1.14) * mm, "end": v(5.5, 1.24) * mm});
            skLineSegment(sketch, "E485", {"start": v(5.5, 1.24) * mm, "end": v(5.67, 1.34) * mm});
            skLineSegment(sketch, "E486", {"start": v(5.67, 1.34) * mm, "end": v(5.84, 1.43) * mm});
            skLineSegment(sketch, "E487", {"start": v(5.84, 1.43) * mm, "end": v(6.01, 1.5) * mm});
            skLineSegment(sketch, "E488", {"start": v(6.01, 1.5) * mm, "end": v(6.2, 1.58) * mm});
            skLineSegment(sketch, "E489", {"start": v(6.2, 1.58) * mm, "end": v(6.37, 1.64) * mm});
            skLineSegment(sketch, "E490", {"start": v(6.37, 1.64) * mm, "end": v(6.56, 1.7) * mm});
            skLineSegment(sketch, "E491", {"start": v(6.56, 1.7) * mm, "end": v(6.76, 1.74) * mm});
            skLineSegment(sketch, "E492", {"start": v(6.76, 1.74) * mm, "end": v(6.96, 1.77) * mm});
            skLineSegment(sketch, "E493", {"start": v(6.96, 1.77) * mm, "end": v(7.16, 1.8) * mm});
            skLineSegment(sketch, "E494", {"start": v(7.16, 1.8) * mm, "end": v(7.37, 1.8) * mm});
            skLineSegment(sketch, "E495", {"start": v(7.37, 1.8) * mm, "end": v(7.59, 1.81) * mm});
            skLineSegment(sketch, "E496", {"start": v(7.59, 1.81) * mm, "end": v(7.8, 1.8) * mm});
            skLineSegment(sketch, "E497", {"start": v(7.8, 1.8) * mm, "end": v(8.01, 1.8) * mm});
            skLineSegment(sketch, "E498", {"start": v(8.01, 1.8) * mm, "end": v(8.22, 1.77) * mm});
            skLineSegment(sketch, "E499", {"start": v(8.22, 1.77) * mm, "end": v(8.42, 1.74) * mm});
            skLineSegment(sketch, "E500", {"start": v(8.42, 1.74) * mm, "end": v(8.61, 1.7) * mm});
            skLineSegment(sketch, "E501", {"start": v(8.61, 1.7) * mm, "end": v(8.8, 1.64) * mm});
            skLineSegment(sketch, "E502", {"start": v(8.8, 1.64) * mm, "end": v(8.99, 1.58) * mm});
            skLineSegment(sketch, "E503", {"start": v(8.99, 1.58) * mm, "end": v(9.16, 1.5) * mm});
            skLineSegment(sketch, "E504", {"start": v(9.16, 1.5) * mm, "end": v(9.34, 1.42) * mm});
            skLineSegment(sketch, "E505", {"start": v(9.34, 1.42) * mm, "end": v(9.5, 1.34) * mm});
            skLineSegment(sketch, "E506", {"start": v(9.5, 1.34) * mm, "end": v(9.67, 1.24) * mm});
            skLineSegment(sketch, "E507", {"start": v(9.67, 1.24) * mm, "end": v(9.83, 1.14) * mm});
            skLineSegment(sketch, "E508", {"start": v(9.83, 1.14) * mm, "end": v(9.98, 1.03) * mm});
            skLineSegment(sketch, "E509", {"start": v(9.98, 1.03) * mm, "end": v(10.13, 0.92) * mm});
            skLineSegment(sketch, "E510", {"start": v(10.13, 0.92) * mm, "end": v(10.27, 0.8) * mm});
            skLineSegment(sketch, "E511", {"start": v(10.27, 0.8) * mm, "end": v(10.4, 0.67) * mm});
            skLineSegment(sketch, "E512", {"start": v(10.4, 0.67) * mm, "end": v(10.52, 0.53) * mm});
            skLineSegment(sketch, "E513", {"start": v(10.52, 0.53) * mm, "end": v(10.64, 0.39) * mm});
            skLineSegment(sketch, "E514", {"start": v(10.64, 0.39) * mm, "end": v(10.76, 0.24) * mm});
            skLineSegment(sketch, "E515", {"start": v(10.76, 0.24) * mm, "end": v(10.86, 0.09) * mm});
            skLineSegment(sketch, "E516", {"start": v(10.86, 0.09) * mm, "end": v(10.96, -0.07) * mm});
            skLineSegment(sketch, "E517", {"start": v(10.96, -0.07) * mm, "end": v(11.05, -0.24) * mm});
            skLineSegment(sketch, "E518", {"start": v(11.05, -0.24) * mm, "end": v(11.14, -0.4) * mm});
            skLineSegment(sketch, "E519", {"start": v(11.14, -0.4) * mm, "end": v(11.21, -0.59) * mm});
            skLineSegment(sketch, "E520", {"start": v(11.21, -0.59) * mm, "end": v(11.28, -0.77) * mm});
            skLineSegment(sketch, "E521", {"start": v(11.28, -0.77) * mm, "end": v(11.34, -0.96) * mm});
            skLineSegment(sketch, "E522", {"start": v(11.34, -0.96) * mm, "end": v(11.4, -1.15) * mm});
            skLineSegment(sketch, "E523", {"start": v(11.4, -1.15) * mm, "end": v(11.44, -1.35) * mm});
            skLineSegment(sketch, "E524", {"start": v(11.44, -1.35) * mm, "end": v(11.47, -1.55) * mm});
            skLineSegment(sketch, "E525", {"start": v(11.47, -1.55) * mm, "end": v(11.5, -1.75) * mm});
            skLineSegment(sketch, "E526", {"start": v(11.5, -1.75) * mm, "end": v(11.5, -1.97) * mm});
            skLineSegment(sketch, "E527", {"start": v(11.5, -1.97) * mm, "end": v(11.51, -2.19) * mm});
            skLineSegment(sketch, "E528", {"start": v(11.51, -2.19) * mm, "end": v(11.5, -2.39) * mm});
            skLineSegment(sketch, "E529", {"start": v(11.5, -2.39) * mm, "end": v(11.5, -2.58) * mm});
            skLineSegment(sketch, "E530", {"start": v(11.5, -2.58) * mm, "end": v(11.47, -2.78) * mm});
            skLineSegment(sketch, "E531", {"start": v(11.47, -2.78) * mm, "end": v(11.44, -2.97) * mm});
            skLineSegment(sketch, "E532", {"start": v(11.44, -2.97) * mm, "end": v(11.4, -3.16) * mm});
            skLineSegment(sketch, "E533", {"start": v(11.4, -3.16) * mm, "end": v(11.36, -3.34) * mm});
            skLineSegment(sketch, "E534", {"start": v(11.36, -3.34) * mm, "end": v(11.3, -3.53) * mm});
            skLineSegment(sketch, "E535", {"start": v(11.3, -3.53) * mm, "end": v(11.23, -3.7) * mm});
            skLineSegment(sketch, "E536", {"start": v(11.23, -3.7) * mm, "end": v(11.17, -3.88) * mm});
            skLineSegment(sketch, "E537", {"start": v(11.17, -3.88) * mm, "end": v(11.09, -4.05) * mm});
            skLineSegment(sketch, "E538", {"start": v(11.09, -4.05) * mm, "end": v(11, -4.21) * mm});
            skLineSegment(sketch, "E539", {"start": v(11, -4.21) * mm, "end": v(10.91, -4.37) * mm});
            skLineSegment(sketch, "E540", {"start": v(10.91, -4.37) * mm, "end": v(10.8, -4.52) * mm});
            skLineSegment(sketch, "E541", {"start": v(10.8, -4.52) * mm, "end": v(10.7, -4.67) * mm});
            skLineSegment(sketch, "E542", {"start": v(10.7, -4.67) * mm, "end": v(10.59, -4.8) * mm});
            skLineSegment(sketch, "E543", {"start": v(10.59, -4.8) * mm, "end": v(10.47, -4.94) * mm});
            skLineSegment(sketch, "E544", {"start": v(10.47, -4.94) * mm, "end": v(10.34, -5.07) * mm});
            skLineSegment(sketch, "E545", {"start": v(10.34, -5.07) * mm, "end": v(10.2, -5.19) * mm});
            skLineSegment(sketch, "E546", {"start": v(10.2, -5.19) * mm, "end": v(10.06, -5.3) * mm});
            skLineSegment(sketch, "E547", {"start": v(10.06, -5.3) * mm, "end": v(9.9, -5.41) * mm});
            skLineSegment(sketch, "E548", {"start": v(9.9, -5.41) * mm, "end": v(9.75, -5.51) * mm});
            skLineSegment(sketch, "E549", {"start": v(9.75, -5.51) * mm, "end": v(9.59, -5.6) * mm});
            skLineSegment(sketch, "E550", {"start": v(9.59, -5.6) * mm, "end": v(9.42, -5.7) * mm});
            skLineSegment(sketch, "E551", {"start": v(9.42, -5.7) * mm, "end": v(9.25, -5.78) * mm});
            skLineSegment(sketch, "E552", {"start": v(9.25, -5.78) * mm, "end": v(8.9, -5.9) * mm});
            skLineSegment(sketch, "E553", {"start": v(8.9, -5.9) * mm, "end": v(8.5, -6) * mm});
            skLineSegment(sketch, "E554", {"start": v(8.5, -6) * mm, "end": v(8.1, -6.06) * mm});
            skLineSegment(sketch, "E555", {"start": v(8.1, -6.06) * mm, "end": v(7.7, -6.08) * mm});
            skLineSegment(sketch, "E556", {"start": v(7.7, -6.08) * mm, "end": v(7.28, -6.07) * mm});
            skLineSegment(sketch, "E557", {"start": v(7.28, -6.07) * mm, "end": v(6.87, -6) * mm});
            skLineSegment(sketch, "E558", {"start": v(6.87, -6) * mm, "end": v(6.47, -5.91) * mm});
            skLineSegment(sketch, "E559", {"start": v(6.47, -5.91) * mm, "end": v(6.1, -5.78) * mm});
            skLineSegment(sketch, "E560", {"start": v(13.65, 3.4) * mm, "end": v(13.37, 3.66) * mm});
            skLineSegment(sketch, "E561", {"start": v(13.37, 3.66) * mm, "end": v(13.07, 3.9) * mm});
            skLineSegment(sketch, "E562", {"start": v(13.07, 3.9) * mm, "end": v(12.75, 4.13) * mm});
            skLineSegment(sketch, "E563", {"start": v(12.75, 4.13) * mm, "end": v(12.43, 4.35) * mm});
            skLineSegment(sketch, "E564", {"start": v(12.43, 4.35) * mm, "end": v(12.09, 4.55) * mm});
            skLineSegment(sketch, "E565", {"start": v(12.09, 4.55) * mm, "end": v(11.74, 4.74) * mm});
            skLineSegment(sketch, "E566", {"start": v(11.74, 4.74) * mm, "end": v(11.37, 4.9) * mm});
            skLineSegment(sketch, "E567", {"start": v(11.37, 4.9) * mm, "end": v(11, 5.07) * mm});
            skLineSegment(sketch, "E568", {"start": v(11, 5.07) * mm, "end": v(10.2, 5.33) * mm});
            skLineSegment(sketch, "E569", {"start": v(10.2, 5.33) * mm, "end": v(9.37, 5.52) * mm});
            skLineSegment(sketch, "E570", {"start": v(9.37, 5.52) * mm, "end": v(8.51, 5.64) * mm});
            skLineSegment(sketch, "E571", {"start": v(8.51, 5.64) * mm, "end": v(7.64, 5.67) * mm});
            skLineSegment(sketch, "E572", {"start": v(7.64, 5.67) * mm, "end": v(6.77, 5.63) * mm});
            skLineSegment(sketch, "E573", {"start": v(6.77, 5.63) * mm, "end": v(5.91, 5.52) * mm});
            skLineSegment(sketch, "E574", {"start": v(5.91, 5.52) * mm, "end": v(5.08, 5.32) * mm});
            skLineSegment(sketch, "E575", {"start": v(5.08, 5.32) * mm, "end": v(4.3, 5.05) * mm});
            skLineSegment(sketch, "E576", {"start": v(4.3, 5.05) * mm, "end": v(3.91, 4.9) * mm});
            skLineSegment(sketch, "E577", {"start": v(3.91, 4.9) * mm, "end": v(3.55, 4.72) * mm});
            skLineSegment(sketch, "E578", {"start": v(3.55, 4.72) * mm, "end": v(3.2, 4.53) * mm});
            skLineSegment(sketch, "E579", {"start": v(3.2, 4.53) * mm, "end": v(2.86, 4.32) * mm});
            skLineSegment(sketch, "E580", {"start": v(2.86, 4.32) * mm, "end": v(2.54, 4.1) * mm});
            skLineSegment(sketch, "E581", {"start": v(2.54, 4.1) * mm, "end": v(2.22, 3.87) * mm});
            skLineSegment(sketch, "E582", {"start": v(2.22, 3.87) * mm, "end": v(1.92, 3.63) * mm});
            skLineSegment(sketch, "E583", {"start": v(1.92, 3.63) * mm, "end": v(1.63, 3.37) * mm});
            skLineSegment(sketch, "E584", {"start": v(1.63, 3.37) * mm, "end": v(1.36, 3.1) * mm});
            skLineSegment(sketch, "E585", {"start": v(1.36, 3.1) * mm, "end": v(1.1, 2.82) * mm});
            skLineSegment(sketch, "E586", {"start": v(1.1, 2.82) * mm, "end": v(0.86, 2.53) * mm});
            skLineSegment(sketch, "E587", {"start": v(0.86, 2.53) * mm, "end": v(0.63, 2.22) * mm});
            skLineSegment(sketch, "E588", {"start": v(0.63, 2.22) * mm, "end": v(0.42, 1.9) * mm});
            skLineSegment(sketch, "E589", {"start": v(0.42, 1.9) * mm, "end": v(0.22, 1.58) * mm});
            skLineSegment(sketch, "E590", {"start": v(0.22, 1.58) * mm, "end": v(0.04, 1.24) * mm});
            skLineSegment(sketch, "E591", {"start": v(0.04, 1.24) * mm, "end": v(-0.13, 0.9) * mm});
            skLineSegment(sketch, "E592", {"start": v(-0.13, 0.9) * mm, "end": v(-0.28, 0.54) * mm});
            skLineSegment(sketch, "E593", {"start": v(-0.28, 0.54) * mm, "end": v(-0.4, 0.18) * mm});
            skLineSegment(sketch, "E594", {"start": v(-0.4, 0.18) * mm, "end": v(-0.52, -0.2) * mm});
            skLineSegment(sketch, "E595", {"start": v(-0.52, -0.2) * mm, "end": v(-0.6, -0.58) * mm});
            skLineSegment(sketch, "E596", {"start": v(-0.6, -0.58) * mm, "end": v(-0.68, -0.97) * mm});
            skLineSegment(sketch, "E597", {"start": v(-0.68, -0.97) * mm, "end": v(-0.73, -1.37) * mm});
            skLineSegment(sketch, "E598", {"start": v(-0.73, -1.37) * mm, "end": v(-0.76, -1.77) * mm});
            skLineSegment(sketch, "E599", {"start": v(-0.76, -1.77) * mm, "end": v(-0.77, -2.19) * mm});
            skLineSegment(sketch, "E600", {"start": v(-0.77, -2.19) * mm, "end": v(-0.76, -2.58) * mm});
            skLineSegment(sketch, "E601", {"start": v(-0.76, -2.58) * mm, "end": v(-0.73, -2.97) * mm});
            skLineSegment(sketch, "E602", {"start": v(-0.73, -2.97) * mm, "end": v(-0.68, -3.35) * mm});
            skLineSegment(sketch, "E603", {"start": v(-0.68, -3.35) * mm, "end": v(-0.61, -3.73) * mm});
            skLineSegment(sketch, "E604", {"start": v(-0.61, -3.73) * mm, "end": v(-0.53, -4.1) * mm});
            skLineSegment(sketch, "E605", {"start": v(-0.53, -4.1) * mm, "end": v(-0.42, -4.47) * mm});
            skLineSegment(sketch, "E606", {"start": v(-0.42, -4.47) * mm, "end": v(-0.29, -4.83) * mm});
            skLineSegment(sketch, "E607", {"start": v(-0.29, -4.83) * mm, "end": v(-0.14, -5.19) * mm});
            skLineSegment(sketch, "E608", {"start": v(-0.14, -5.19) * mm, "end": v(0.02, -5.54) * mm});
            skLineSegment(sketch, "E609", {"start": v(0.02, -5.54) * mm, "end": v(0.2, -5.87) * mm});
            skLineSegment(sketch, "E610", {"start": v(0.2, -5.87) * mm, "end": v(0.4, -6.2) * mm});
            skLineSegment(sketch, "E611", {"start": v(0.4, -6.2) * mm, "end": v(0.6, -6.51) * mm});
            skLineSegment(sketch, "E612", {"start": v(0.6, -6.51) * mm, "end": v(0.84, -6.82) * mm});
            skLineSegment(sketch, "E613", {"start": v(0.84, -6.82) * mm, "end": v(1.08, -7.1) * mm});
            skLineSegment(sketch, "E614", {"start": v(1.08, -7.1) * mm, "end": v(1.33, -7.39) * mm});
            skLineSegment(sketch, "E615", {"start": v(1.33, -7.39) * mm, "end": v(1.6, -7.66) * mm});
            skLineSegment(sketch, "E616", {"start": v(1.6, -7.66) * mm, "end": v(1.9, -7.91) * mm});
            skLineSegment(sketch, "E617", {"start": v(1.9, -7.91) * mm, "end": v(2.2, -8.15) * mm});
            skLineSegment(sketch, "E618", {"start": v(2.2, -8.15) * mm, "end": v(2.5, -8.38) * mm});
            skLineSegment(sketch, "E619", {"start": v(2.5, -8.38) * mm, "end": v(2.84, -8.6) * mm});
            skLineSegment(sketch, "E620", {"start": v(2.84, -8.6) * mm, "end": v(3.17, -8.8) * mm});
            skLineSegment(sketch, "E621", {"start": v(3.17, -8.8) * mm, "end": v(3.53, -8.98) * mm});
            skLineSegment(sketch, "E622", {"start": v(3.53, -8.98) * mm, "end": v(3.89, -9.15) * mm});
            skLineSegment(sketch, "E623", {"start": v(3.89, -9.15) * mm, "end": v(4.26, -9.31) * mm});
            skLineSegment(sketch, "E624", {"start": v(4.26, -9.31) * mm, "end": v(4.65, -9.45) * mm});
            skLineSegment(sketch, "E625", {"start": v(4.65, -9.45) * mm, "end": v(5.05, -9.58) * mm});
            skLineSegment(sketch, "E626", {"start": v(5.05, -9.58) * mm, "end": v(5.45, -9.68) * mm});
            skLineSegment(sketch, "E627", {"start": v(5.45, -9.68) * mm, "end": v(5.87, -9.77) * mm});
            skLineSegment(sketch, "E628", {"start": v(5.87, -9.77) * mm, "end": v(6.29, -9.83) * mm});
            skLineSegment(sketch, "E629", {"start": v(6.29, -9.83) * mm, "end": v(6.71, -9.88) * mm});
            skLineSegment(sketch, "E630", {"start": v(6.71, -9.88) * mm, "end": v(7.15, -9.91) * mm});
            skLineSegment(sketch, "E631", {"start": v(7.15, -9.91) * mm, "end": v(7.59, -9.92) * mm});
            skLineSegment(sketch, "E632", {"start": v(7.59, -9.92) * mm, "end": v(8.04, -9.91) * mm});
            skLineSegment(sketch, "E633", {"start": v(8.04, -9.91) * mm, "end": v(8.48, -9.88) * mm});
            skLineSegment(sketch, "E634", {"start": v(8.48, -9.88) * mm, "end": v(8.9, -9.83) * mm});
            skLineSegment(sketch, "E635", {"start": v(8.9, -9.83) * mm, "end": v(9.33, -9.76) * mm});
            skLineSegment(sketch, "E636", {"start": v(9.33, -9.76) * mm, "end": v(9.75, -9.68) * mm});
            skLineSegment(sketch, "E637", {"start": v(9.75, -9.68) * mm, "end": v(10.16, -9.57) * mm});
            skLineSegment(sketch, "E638", {"start": v(10.16, -9.57) * mm, "end": v(10.56, -9.44) * mm});
            skLineSegment(sketch, "E639", {"start": v(10.56, -9.44) * mm, "end": v(10.95, -9.3) * mm});
            skLineSegment(sketch, "E640", {"start": v(10.95, -9.3) * mm, "end": v(11.33, -9.13) * mm});
            skLineSegment(sketch, "E641", {"start": v(11.33, -9.13) * mm, "end": v(11.7, -8.96) * mm});
            skLineSegment(sketch, "E642", {"start": v(11.7, -8.96) * mm, "end": v(12.06, -8.77) * mm});
            skLineSegment(sketch, "E643", {"start": v(12.06, -8.77) * mm, "end": v(12.4, -8.56) * mm});
            skLineSegment(sketch, "E644", {"start": v(12.4, -8.56) * mm, "end": v(12.73, -8.35) * mm});
            skLineSegment(sketch, "E645", {"start": v(12.73, -8.35) * mm, "end": v(13.04, -8.12) * mm});
            skLineSegment(sketch, "E646", {"start": v(13.04, -8.12) * mm, "end": v(13.34, -7.87) * mm});
            skLineSegment(sketch, "E647", {"start": v(13.34, -7.87) * mm, "end": v(13.63, -7.61) * mm});
            skLineSegment(sketch, "E648", {"start": v(13.63, -7.61) * mm, "end": v(13.9, -7.34) * mm});
            skLineSegment(sketch, "E649", {"start": v(13.9, -7.34) * mm, "end": v(14.16, -7.06) * mm});
            skLineSegment(sketch, "E650", {"start": v(14.16, -7.06) * mm, "end": v(14.4, -6.77) * mm});
            skLineSegment(sketch, "E651", {"start": v(14.4, -6.77) * mm, "end": v(14.63, -6.46) * mm});
            skLineSegment(sketch, "E652", {"start": v(14.63, -6.46) * mm, "end": v(14.84, -6.15) * mm});
            skLineSegment(sketch, "E653", {"start": v(14.84, -6.15) * mm, "end": v(15.04, -5.82) * mm});
            skLineSegment(sketch, "E654", {"start": v(15.04, -5.82) * mm, "end": v(15.22, -5.49) * mm});
            skLineSegment(sketch, "E655", {"start": v(15.22, -5.49) * mm, "end": v(15.39, -5.14) * mm});
            skLineSegment(sketch, "E656", {"start": v(15.39, -5.14) * mm, "end": v(15.54, -4.79) * mm});
            skLineSegment(sketch, "E657", {"start": v(15.54, -4.79) * mm, "end": v(15.67, -4.42) * mm});
            skLineSegment(sketch, "E658", {"start": v(15.67, -4.42) * mm, "end": v(15.78, -4.05) * mm});
            skLineSegment(sketch, "E659", {"start": v(15.78, -4.05) * mm, "end": v(15.87, -3.67) * mm});
            skLineSegment(sketch, "E660", {"start": v(15.87, -3.67) * mm, "end": v(15.94, -3.29) * mm});
            skLineSegment(sketch, "E661", {"start": v(15.94, -3.29) * mm, "end": v(15.99, -2.9) * mm});
            skLineSegment(sketch, "E662", {"start": v(15.99, -2.9) * mm, "end": v(16.02, -2.5) * mm});
            skLineSegment(sketch, "E663", {"start": v(16.02, -2.5) * mm, "end": v(16.03, -2.08) * mm});
            skLineSegment(sketch, "E664", {"start": v(16.03, -2.08) * mm, "end": v(16.02, -1.68) * mm});
            skLineSegment(sketch, "E665", {"start": v(16.02, -1.68) * mm, "end": v(16, -1.29) * mm});
            skLineSegment(sketch, "E666", {"start": v(16, -1.29) * mm, "end": v(15.94, -0.9) * mm});
            skLineSegment(sketch, "E667", {"start": v(15.94, -0.9) * mm, "end": v(15.87, -0.52) * mm});
            skLineSegment(sketch, "E668", {"start": v(15.87, -0.52) * mm, "end": v(15.79, -0.15) * mm});
            skLineSegment(sketch, "E669", {"start": v(15.79, -0.15) * mm, "end": v(15.68, 0.22) * mm});
            skLineSegment(sketch, "E670", {"start": v(15.68, 0.22) * mm, "end": v(15.55, 0.58) * mm});
            skLineSegment(sketch, "E671", {"start": v(15.55, 0.58) * mm, "end": v(15.4, 0.93) * mm});
            skLineSegment(sketch, "E672", {"start": v(15.4, 0.93) * mm, "end": v(15.24, 1.28) * mm});
            skLineSegment(sketch, "E673", {"start": v(15.24, 1.28) * mm, "end": v(15.06, 1.61) * mm});
            skLineSegment(sketch, "E674", {"start": v(15.06, 1.61) * mm, "end": v(14.86, 1.94) * mm});
            skLineSegment(sketch, "E675", {"start": v(14.86, 1.94) * mm, "end": v(14.65, 2.25) * mm});
            skLineSegment(sketch, "E676", {"start": v(14.65, 2.25) * mm, "end": v(14.42, 2.55) * mm});
            skLineSegment(sketch, "E677", {"start": v(14.42, 2.55) * mm, "end": v(14.18, 2.84) * mm});
            skLineSegment(sketch, "E678", {"start": v(14.18, 2.84) * mm, "end": v(13.93, 3.13) * mm});
            skLineSegment(sketch, "E679", {"start": v(13.93, 3.13) * mm, "end": v(13.65, 3.4) * mm});
            skLineSegment(sketch, "E680", {"start": v(25.08, -3.83) * mm, "end": v(24.63, -2.68) * mm});
            skLineSegment(sketch, "E681", {"start": v(24.63, -2.68) * mm, "end": v(24.19, -1.53) * mm});
            skLineSegment(sketch, "E682", {"start": v(24.19, -1.53) * mm, "end": v(23.74, -0.37) * mm});
            skLineSegment(sketch, "E683", {"start": v(23.74, -0.37) * mm, "end": v(23.3, 0.78) * mm});
            skLineSegment(sketch, "E684", {"start": v(23.3, 0.78) * mm, "end": v(22.85, 1.93) * mm});
            skLineSegment(sketch, "E685", {"start": v(22.85, 1.93) * mm, "end": v(22.4, 3.08) * mm});
            skLineSegment(sketch, "E686", {"start": v(22.4, 3.08) * mm, "end": v(21.96, 4.24) * mm});
            skLineSegment(sketch, "E687", {"start": v(21.96, 4.24) * mm, "end": v(21.51, 5.39) * mm});
            skLineSegment(sketch, "E688", {"start": v(21.51, 5.39) * mm, "end": v(20.9, 5.39) * mm});
            skLineSegment(sketch, "E689", {"start": v(20.9, 5.39) * mm, "end": v(20.3, 5.39) * mm});
            skLineSegment(sketch, "E690", {"start": v(20.3, 5.39) * mm, "end": v(19.7, 5.39) * mm});
            skLineSegment(sketch, "E691", {"start": v(19.7, 5.39) * mm, "end": v(19.09, 5.39) * mm});
            skLineSegment(sketch, "E692", {"start": v(19.09, 5.39) * mm, "end": v(18.48, 5.39) * mm});
            skLineSegment(sketch, "E693", {"start": v(18.48, 5.39) * mm, "end": v(17.88, 5.39) * mm});
            skLineSegment(sketch, "E694", {"start": v(17.88, 5.39) * mm, "end": v(17.27, 5.39) * mm});
            skLineSegment(sketch, "E695", {"start": v(17.27, 5.39) * mm, "end": v(16.67, 5.39) * mm});
            skLineSegment(sketch, "E696", {"start": v(16.67, 5.39) * mm, "end": v(17.48, 3.5) * mm});
            skLineSegment(sketch, "E697", {"start": v(17.48, 3.5) * mm, "end": v(18.3, 1.61) * mm});
            skLineSegment(sketch, "E698", {"start": v(18.3, 1.61) * mm, "end": v(19.1, -0.27) * mm});
            skLineSegment(sketch, "E699", {"start": v(19.1, -0.27) * mm, "end": v(19.92, -2.16) * mm});
            skLineSegment(sketch, "E700", {"start": v(19.92, -2.16) * mm, "end": v(20.73, -4.05) * mm});
            skLineSegment(sketch, "E701", {"start": v(20.73, -4.05) * mm, "end": v(21.54, -5.93) * mm});
            skLineSegment(sketch, "E702", {"start": v(21.54, -5.93) * mm, "end": v(22.36, -7.82) * mm});
            skLineSegment(sketch, "E703", {"start": v(22.36, -7.82) * mm, "end": v(23.17, -9.7) * mm});
            skLineSegment(sketch, "E704", {"start": v(23.17, -9.7) * mm, "end": v(23.64, -9.7) * mm});
            skLineSegment(sketch, "E705", {"start": v(23.64, -9.7) * mm, "end": v(24.12, -9.7) * mm});
            skLineSegment(sketch, "E706", {"start": v(24.12, -9.7) * mm, "end": v(24.59, -9.7) * mm});
            skLineSegment(sketch, "E707", {"start": v(24.59, -9.7) * mm, "end": v(25.06, -9.7) * mm});
            skLineSegment(sketch, "E708", {"start": v(25.06, -9.7) * mm, "end": v(25.53, -9.7) * mm});
            skLineSegment(sketch, "E709", {"start": v(25.53, -9.7) * mm, "end": v(26, -9.7) * mm});
            skLineSegment(sketch, "E710", {"start": v(26, -9.7) * mm, "end": v(26.48, -9.7) * mm});
            skLineSegment(sketch, "E711", {"start": v(26.48, -9.7) * mm, "end": v(26.95, -9.7) * mm});
            skLineSegment(sketch, "E712", {"start": v(26.95, -9.7) * mm, "end": v(27.76, -7.82) * mm});
            skLineSegment(sketch, "E713", {"start": v(27.76, -7.82) * mm, "end": v(28.57, -5.93) * mm});
            skLineSegment(sketch, "E714", {"start": v(28.57, -5.93) * mm, "end": v(29.38, -4.05) * mm});
            skLineSegment(sketch, "E715", {"start": v(29.38, -4.05) * mm, "end": v(30.2, -2.16) * mm});
            skLineSegment(sketch, "E716", {"start": v(30.2, -2.16) * mm, "end": v(31, -0.27) * mm});
            skLineSegment(sketch, "E717", {"start": v(31, -0.27) * mm, "end": v(31.8, 1.61) * mm});
            skLineSegment(sketch, "E718", {"start": v(31.8, 1.61) * mm, "end": v(32.62, 3.5) * mm});
            skLineSegment(sketch, "E719", {"start": v(32.62, 3.5) * mm, "end": v(33.43, 5.39) * mm});
            skLineSegment(sketch, "E720", {"start": v(33.43, 5.39) * mm, "end": v(32.83, 5.39) * mm});
            skLineSegment(sketch, "E721", {"start": v(32.83, 5.39) * mm, "end": v(32.24, 5.39) * mm});
            skLineSegment(sketch, "E722", {"start": v(32.24, 5.39) * mm, "end": v(31.64, 5.39) * mm});
            skLineSegment(sketch, "E723", {"start": v(31.64, 5.39) * mm, "end": v(31.05, 5.39) * mm});
            skLineSegment(sketch, "E724", {"start": v(31.05, 5.39) * mm, "end": v(30.45, 5.39) * mm});
            skLineSegment(sketch, "E725", {"start": v(30.45, 5.39) * mm, "end": v(29.86, 5.39) * mm});
            skLineSegment(sketch, "E726", {"start": v(29.86, 5.39) * mm, "end": v(29.26, 5.39) * mm});
            skLineSegment(sketch, "E727", {"start": v(29.26, 5.39) * mm, "end": v(28.66, 5.39) * mm});
            skLineSegment(sketch, "E728", {"start": v(28.66, 5.39) * mm, "end": v(28.22, 4.24) * mm});
            skLineSegment(sketch, "E729", {"start": v(28.22, 4.24) * mm, "end": v(27.77, 3.08) * mm});
            skLineSegment(sketch, "E730", {"start": v(27.77, 3.08) * mm, "end": v(27.32, 1.93) * mm});
            skLineSegment(sketch, "E731", {"start": v(27.32, 1.93) * mm, "end": v(26.87, 0.78) * mm});
            skLineSegment(sketch, "E732", {"start": v(26.87, 0.78) * mm, "end": v(26.42, -0.37) * mm});
            skLineSegment(sketch, "E733", {"start": v(26.42, -0.37) * mm, "end": v(25.97, -1.53) * mm});
            skLineSegment(sketch, "E734", {"start": v(25.97, -1.53) * mm, "end": v(25.53, -2.68) * mm});
            skLineSegment(sketch, "E735", {"start": v(25.53, -2.68) * mm, "end": v(25.08, -3.83) * mm});
            skLineSegment(sketch, "E736", {"start": v(40.96, -5.78) * mm, "end": v(40.79, -5.7) * mm});
            skLineSegment(sketch, "E737", {"start": v(40.79, -5.7) * mm, "end": v(40.62, -5.6) * mm});
            skLineSegment(sketch, "E738", {"start": v(40.62, -5.6) * mm, "end": v(40.45, -5.51) * mm});
            skLineSegment(sketch, "E739", {"start": v(40.45, -5.51) * mm, "end": v(40.3, -5.4) * mm});
            skLineSegment(sketch, "E740", {"start": v(40.3, -5.4) * mm, "end": v(40.14, -5.3) * mm});
            skLineSegment(sketch, "E741", {"start": v(40.14, -5.3) * mm, "end": v(40, -5.18) * mm});
            skLineSegment(sketch, "E742", {"start": v(40, -5.18) * mm, "end": v(39.86, -5.06) * mm});
            skLineSegment(sketch, "E743", {"start": v(39.86, -5.06) * mm, "end": v(39.73, -4.93) * mm});
            skLineSegment(sketch, "E744", {"start": v(39.73, -4.93) * mm, "end": v(39.6, -4.79) * mm});
            skLineSegment(sketch, "E745", {"start": v(39.6, -4.79) * mm, "end": v(39.48, -4.64) * mm});
            skLineSegment(sketch, "E746", {"start": v(39.48, -4.64) * mm, "end": v(39.36, -4.5) * mm});
            skLineSegment(sketch, "E747", {"start": v(39.36, -4.5) * mm, "end": v(39.26, -4.34) * mm});
            skLineSegment(sketch, "E748", {"start": v(39.26, -4.34) * mm, "end": v(39.16, -4.18) * mm});
            skLineSegment(sketch, "E749", {"start": v(39.16, -4.18) * mm, "end": v(39.07, -4.01) * mm});
            skLineSegment(sketch, "E750", {"start": v(39.07, -4.01) * mm, "end": v(38.99, -3.84) * mm});
            skLineSegment(sketch, "E751", {"start": v(38.99, -3.84) * mm, "end": v(38.9, -3.67) * mm});
            skLineSegment(sketch, "E752", {"start": v(38.9, -3.67) * mm, "end": v(38.84, -3.5) * mm});
            skLineSegment(sketch, "E753", {"start": v(38.84, -3.5) * mm, "end": v(38.78, -3.3) * mm});
            skLineSegment(sketch, "E754", {"start": v(38.78, -3.3) * mm, "end": v(38.73, -3.12) * mm});
            skLineSegment(sketch, "E755", {"start": v(38.73, -3.12) * mm, "end": v(38.7, -2.92) * mm});
            skLineSegment(sketch, "E756", {"start": v(38.7, -2.92) * mm, "end": v(38.66, -2.72) * mm});
            skLineSegment(sketch, "E757", {"start": v(38.66, -2.72) * mm, "end": v(38.64, -2.52) * mm});
            skLineSegment(sketch, "E758", {"start": v(38.64, -2.52) * mm, "end": v(38.62, -2.3) * mm});
            skLineSegment(sketch, "E759", {"start": v(38.62, -2.3) * mm, "end": v(38.62, -2.08) * mm});
            skLineSegment(sketch, "E760", {"start": v(38.62, -2.08) * mm, "end": v(38.62, -1.88) * mm});
            skLineSegment(sketch, "E761", {"start": v(38.62, -1.88) * mm, "end": v(38.63, -1.69) * mm});
            skLineSegment(sketch, "E762", {"start": v(38.63, -1.69) * mm, "end": v(38.65, -1.49) * mm});
            skLineSegment(sketch, "E763", {"start": v(38.65, -1.49) * mm, "end": v(38.68, -1.3) * mm});
            skLineSegment(sketch, "E764", {"start": v(38.68, -1.3) * mm, "end": v(38.72, -1.1) * mm});
            skLineSegment(sketch, "E765", {"start": v(38.72, -1.1) * mm, "end": v(38.77, -0.92) * mm});
            skLineSegment(sketch, "E766", {"start": v(38.77, -0.92) * mm, "end": v(38.82, -0.73) * mm});
            skLineSegment(sketch, "E767", {"start": v(38.82, -0.73) * mm, "end": v(38.89, -0.55) * mm});
            skLineSegment(sketch, "E768", {"start": v(38.89, -0.55) * mm, "end": v(38.96, -0.37) * mm});
            skLineSegment(sketch, "E769", {"start": v(38.96, -0.37) * mm, "end": v(39.04, -0.2) * mm});
            skLineSegment(sketch, "E770", {"start": v(39.04, -0.2) * mm, "end": v(39.12, -0.04) * mm});
            skLineSegment(sketch, "E771", {"start": v(39.12, -0.04) * mm, "end": v(39.21, 0.12) * mm});
            skLineSegment(sketch, "E772", {"start": v(39.21, 0.12) * mm, "end": v(39.31, 0.27) * mm});
            skLineSegment(sketch, "E773", {"start": v(39.31, 0.27) * mm, "end": v(39.42, 0.4) * mm});
            skLineSegment(sketch, "E774", {"start": v(39.42, 0.4) * mm, "end": v(39.53, 0.55) * mm});
            skLineSegment(sketch, "E775", {"start": v(39.53, 0.55) * mm, "end": v(39.65, 0.68) * mm});
            skLineSegment(sketch, "E776", {"start": v(39.65, 0.68) * mm, "end": v(39.78, 0.8) * mm});
            skLineSegment(sketch, "E777", {"start": v(39.78, 0.8) * mm, "end": v(39.92, 0.92) * mm});
            skLineSegment(sketch, "E778", {"start": v(39.92, 0.92) * mm, "end": v(40.06, 1.04) * mm});
            skLineSegment(sketch, "E779", {"start": v(40.06, 1.04) * mm, "end": v(40.21, 1.14) * mm});
            skLineSegment(sketch, "E780", {"start": v(40.21, 1.14) * mm, "end": v(40.37, 1.24) * mm});
            skLineSegment(sketch, "E781", {"start": v(40.37, 1.24) * mm, "end": v(40.53, 1.34) * mm});
            skLineSegment(sketch, "E782", {"start": v(40.53, 1.34) * mm, "end": v(40.7, 1.43) * mm});
            skLineSegment(sketch, "E783", {"start": v(40.7, 1.43) * mm, "end": v(40.87, 1.5) * mm});
            skLineSegment(sketch, "E784", {"start": v(40.87, 1.5) * mm, "end": v(41.05, 1.58) * mm});
            skLineSegment(sketch, "E785", {"start": v(41.05, 1.58) * mm, "end": v(41.23, 1.64) * mm});
            skLineSegment(sketch, "E786", {"start": v(41.23, 1.64) * mm, "end": v(41.42, 1.7) * mm});
            skLineSegment(sketch, "E787", {"start": v(41.42, 1.7) * mm, "end": v(41.62, 1.74) * mm});
            skLineSegment(sketch, "E788", {"start": v(41.62, 1.74) * mm, "end": v(41.82, 1.77) * mm});
            skLineSegment(sketch, "E789", {"start": v(41.82, 1.77) * mm, "end": v(42.03, 1.8) * mm});
            skLineSegment(sketch, "E790", {"start": v(42.03, 1.8) * mm, "end": v(42.24, 1.8) * mm});
            skLineSegment(sketch, "E791", {"start": v(42.24, 1.8) * mm, "end": v(42.45, 1.81) * mm});
            skLineSegment(sketch, "E792", {"start": v(42.45, 1.81) * mm, "end": v(42.67, 1.8) * mm});
            skLineSegment(sketch, "E793", {"start": v(42.67, 1.8) * mm, "end": v(42.88, 1.8) * mm});
            skLineSegment(sketch, "E794", {"start": v(42.88, 1.8) * mm, "end": v(43.08, 1.77) * mm});
            skLineSegment(sketch, "E795", {"start": v(43.08, 1.77) * mm, "end": v(43.28, 1.74) * mm});
            skLineSegment(sketch, "E796", {"start": v(43.28, 1.74) * mm, "end": v(43.48, 1.7) * mm});
            skLineSegment(sketch, "E797", {"start": v(43.48, 1.7) * mm, "end": v(43.67, 1.64) * mm});
            skLineSegment(sketch, "E798", {"start": v(43.67, 1.64) * mm, "end": v(43.85, 1.58) * mm});
            skLineSegment(sketch, "E799", {"start": v(43.85, 1.58) * mm, "end": v(44.03, 1.5) * mm});
            skLineSegment(sketch, "E800", {"start": v(44.03, 1.5) * mm, "end": v(44.2, 1.43) * mm});
            skLineSegment(sketch, "E801", {"start": v(44.2, 1.43) * mm, "end": v(44.37, 1.34) * mm});
            skLineSegment(sketch, "E802", {"start": v(44.37, 1.34) * mm, "end": v(44.54, 1.24) * mm});
            skLineSegment(sketch, "E803", {"start": v(44.54, 1.24) * mm, "end": v(44.7, 1.14) * mm});
            skLineSegment(sketch, "E804", {"start": v(44.7, 1.14) * mm, "end": v(44.84, 1.03) * mm});
            skLineSegment(sketch, "E805", {"start": v(44.84, 1.03) * mm, "end": v(44.99, 0.92) * mm});
            skLineSegment(sketch, "E806", {"start": v(44.99, 0.92) * mm, "end": v(45.13, 0.8) * mm});
            skLineSegment(sketch, "E807", {"start": v(45.13, 0.8) * mm, "end": v(45.26, 0.67) * mm});
            skLineSegment(sketch, "E808", {"start": v(45.26, 0.67) * mm, "end": v(45.39, 0.53) * mm});
            skLineSegment(sketch, "E809", {"start": v(45.39, 0.53) * mm, "end": v(45.5, 0.39) * mm});
            skLineSegment(sketch, "E810", {"start": v(45.5, 0.39) * mm, "end": v(45.62, 0.24) * mm});
            skLineSegment(sketch, "E811", {"start": v(45.62, 0.24) * mm, "end": v(45.73, 0.09) * mm});
            skLineSegment(sketch, "E812", {"start": v(45.73, 0.09) * mm, "end": v(45.82, -0.07) * mm});
            skLineSegment(sketch, "E813", {"start": v(45.82, -0.07) * mm, "end": v(45.92, -0.24) * mm});
            skLineSegment(sketch, "E814", {"start": v(45.92, -0.24) * mm, "end": v(46, -0.4) * mm});
            skLineSegment(sketch, "E815", {"start": v(46, -0.4) * mm, "end": v(46.08, -0.59) * mm});
            skLineSegment(sketch, "E816", {"start": v(46.08, -0.59) * mm, "end": v(46.15, -0.77) * mm});
            skLineSegment(sketch, "E817", {"start": v(46.15, -0.77) * mm, "end": v(46.2, -0.96) * mm});
            skLineSegment(sketch, "E818", {"start": v(46.2, -0.96) * mm, "end": v(46.26, -1.15) * mm});
            skLineSegment(sketch, "E819", {"start": v(46.26, -1.15) * mm, "end": v(46.3, -1.34) * mm});
            skLineSegment(sketch, "E820", {"start": v(46.3, -1.34) * mm, "end": v(46.33, -1.55) * mm});
            skLineSegment(sketch, "E821", {"start": v(46.33, -1.55) * mm, "end": v(46.35, -1.75) * mm});
            skLineSegment(sketch, "E822", {"start": v(46.35, -1.75) * mm, "end": v(46.37, -1.97) * mm});
            skLineSegment(sketch, "E823", {"start": v(46.37, -1.97) * mm, "end": v(46.37, -2.19) * mm});
            skLineSegment(sketch, "E824", {"start": v(46.37, -2.19) * mm, "end": v(46.37, -2.39) * mm});
            skLineSegment(sketch, "E825", {"start": v(46.37, -2.39) * mm, "end": v(46.35, -2.58) * mm});
            skLineSegment(sketch, "E826", {"start": v(46.35, -2.58) * mm, "end": v(46.33, -2.78) * mm});
            skLineSegment(sketch, "E827", {"start": v(46.33, -2.78) * mm, "end": v(46.3, -2.97) * mm});
            skLineSegment(sketch, "E828", {"start": v(46.3, -2.97) * mm, "end": v(46.26, -3.16) * mm});
            skLineSegment(sketch, "E829", {"start": v(46.26, -3.16) * mm, "end": v(46.22, -3.34) * mm});
            skLineSegment(sketch, "E830", {"start": v(46.22, -3.34) * mm, "end": v(46.16, -3.53) * mm});
            skLineSegment(sketch, "E831", {"start": v(46.16, -3.53) * mm, "end": v(46.1, -3.7) * mm});
            skLineSegment(sketch, "E832", {"start": v(46.1, -3.7) * mm, "end": v(46.03, -3.88) * mm});
            skLineSegment(sketch, "E833", {"start": v(46.03, -3.88) * mm, "end": v(45.95, -4.05) * mm});
            skLineSegment(sketch, "E834", {"start": v(45.95, -4.05) * mm, "end": v(45.87, -4.21) * mm});
            skLineSegment(sketch, "E835", {"start": v(45.87, -4.21) * mm, "end": v(45.77, -4.37) * mm});
            skLineSegment(sketch, "E836", {"start": v(45.77, -4.37) * mm, "end": v(45.67, -4.52) * mm});
            skLineSegment(sketch, "E837", {"start": v(45.67, -4.52) * mm, "end": v(45.56, -4.67) * mm});
            skLineSegment(sketch, "E838", {"start": v(45.56, -4.67) * mm, "end": v(45.45, -4.8) * mm});
            skLineSegment(sketch, "E839", {"start": v(45.45, -4.8) * mm, "end": v(45.32, -4.94) * mm});
            skLineSegment(sketch, "E840", {"start": v(45.32, -4.94) * mm, "end": v(45.2, -5.07) * mm});
            skLineSegment(sketch, "E841", {"start": v(45.2, -5.07) * mm, "end": v(45.06, -5.19) * mm});
            skLineSegment(sketch, "E842", {"start": v(45.06, -5.19) * mm, "end": v(44.92, -5.3) * mm});
            skLineSegment(sketch, "E843", {"start": v(44.92, -5.3) * mm, "end": v(44.77, -5.41) * mm});
            skLineSegment(sketch, "E844", {"start": v(44.77, -5.41) * mm, "end": v(44.61, -5.51) * mm});
            skLineSegment(sketch, "E845", {"start": v(44.61, -5.51) * mm, "end": v(44.45, -5.6) * mm});
            skLineSegment(sketch, "E846", {"start": v(44.45, -5.6) * mm, "end": v(44.28, -5.7) * mm});
            skLineSegment(sketch, "E847", {"start": v(44.28, -5.7) * mm, "end": v(44.1, -5.78) * mm});
            skLineSegment(sketch, "E848", {"start": v(44.1, -5.78) * mm, "end": v(43.75, -5.9) * mm});
            skLineSegment(sketch, "E849", {"start": v(43.75, -5.9) * mm, "end": v(43.37, -6) * mm});
            skLineSegment(sketch, "E850", {"start": v(43.37, -6) * mm, "end": v(42.97, -6.06) * mm});
            skLineSegment(sketch, "E851", {"start": v(42.97, -6.06) * mm, "end": v(42.56, -6.08) * mm});
            skLineSegment(sketch, "E852", {"start": v(42.56, -6.08) * mm, "end": v(42.14, -6.06) * mm});
            skLineSegment(sketch, "E853", {"start": v(42.14, -6.06) * mm, "end": v(41.73, -6) * mm});
            skLineSegment(sketch, "E854", {"start": v(41.73, -6) * mm, "end": v(41.33, -5.91) * mm});
            skLineSegment(sketch, "E855", {"start": v(41.33, -5.91) * mm, "end": v(40.96, -5.78) * mm});
            skLineSegment(sketch, "E856", {"start": v(50.27, 0.93) * mm, "end": v(50.1, 1.28) * mm});
            skLineSegment(sketch, "E857", {"start": v(50.1, 1.28) * mm, "end": v(49.92, 1.61) * mm});
            skLineSegment(sketch, "E858", {"start": v(49.92, 1.61) * mm, "end": v(49.73, 1.94) * mm});
            skLineSegment(sketch, "E859", {"start": v(49.73, 1.94) * mm, "end": v(49.52, 2.25) * mm});
            skLineSegment(sketch, "E860", {"start": v(49.52, 2.25) * mm, "end": v(49.29, 2.55) * mm});
            skLineSegment(sketch, "E861", {"start": v(49.29, 2.55) * mm, "end": v(49.05, 2.84) * mm});
            skLineSegment(sketch, "E862", {"start": v(49.05, 2.84) * mm, "end": v(48.79, 3.13) * mm});
            skLineSegment(sketch, "E863", {"start": v(48.79, 3.13) * mm, "end": v(48.52, 3.4) * mm});
            skLineSegment(sketch, "E864", {"start": v(48.52, 3.4) * mm, "end": v(48.23, 3.65) * mm});
            skLineSegment(sketch, "E865", {"start": v(48.23, 3.65) * mm, "end": v(47.93, 3.9) * mm});
            skLineSegment(sketch, "E866", {"start": v(47.93, 3.9) * mm, "end": v(47.62, 4.13) * mm});
            skLineSegment(sketch, "E867", {"start": v(47.62, 4.13) * mm, "end": v(47.3, 4.35) * mm});
            skLineSegment(sketch, "E868", {"start": v(47.3, 4.35) * mm, "end": v(46.95, 4.55) * mm});
            skLineSegment(sketch, "E869", {"start": v(46.95, 4.55) * mm, "end": v(46.6, 4.74) * mm});
            skLineSegment(sketch, "E870", {"start": v(46.6, 4.74) * mm, "end": v(46.23, 4.9) * mm});
            skLineSegment(sketch, "E871", {"start": v(46.23, 4.9) * mm, "end": v(45.86, 5.07) * mm});
            skLineSegment(sketch, "E872", {"start": v(45.86, 5.07) * mm, "end": v(45.07, 5.33) * mm});
            skLineSegment(sketch, "E873", {"start": v(45.07, 5.33) * mm, "end": v(44.24, 5.52) * mm});
            skLineSegment(sketch, "E874", {"start": v(44.24, 5.52) * mm, "end": v(43.38, 5.64) * mm});
            skLineSegment(sketch, "E875", {"start": v(43.38, 5.64) * mm, "end": v(42.5, 5.67) * mm});
            skLineSegment(sketch, "E876", {"start": v(42.5, 5.67) * mm, "end": v(41.64, 5.63) * mm});
            skLineSegment(sketch, "E877", {"start": v(41.64, 5.63) * mm, "end": v(40.78, 5.52) * mm});
            skLineSegment(sketch, "E878", {"start": v(40.78, 5.52) * mm, "end": v(39.94, 5.32) * mm});
            skLineSegment(sketch, "E879", {"start": v(39.94, 5.32) * mm, "end": v(39.15, 5.05) * mm});
            skLineSegment(sketch, "E880", {"start": v(39.15, 5.05) * mm, "end": v(38.78, 4.9) * mm});
            skLineSegment(sketch, "E881", {"start": v(38.78, 4.9) * mm, "end": v(38.41, 4.72) * mm});
            skLineSegment(sketch, "E882", {"start": v(38.41, 4.72) * mm, "end": v(38.06, 4.53) * mm});
            skLineSegment(sketch, "E883", {"start": v(38.06, 4.53) * mm, "end": v(37.72, 4.32) * mm});
            skLineSegment(sketch, "E884", {"start": v(37.72, 4.32) * mm, "end": v(37.4, 4.1) * mm});
            skLineSegment(sketch, "E885", {"start": v(37.4, 4.1) * mm, "end": v(37.09, 3.87) * mm});
            skLineSegment(sketch, "E886", {"start": v(37.09, 3.87) * mm, "end": v(36.79, 3.63) * mm});
            skLineSegment(sketch, "E887", {"start": v(36.79, 3.63) * mm, "end": v(36.5, 3.37) * mm});
            skLineSegment(sketch, "E888", {"start": v(36.5, 3.37) * mm, "end": v(36.23, 3.1) * mm});
            skLineSegment(sketch, "E889", {"start": v(36.23, 3.1) * mm, "end": v(35.97, 2.82) * mm});
            skLineSegment(sketch, "E890", {"start": v(35.97, 2.82) * mm, "end": v(35.73, 2.53) * mm});
            skLineSegment(sketch, "E891", {"start": v(35.73, 2.53) * mm, "end": v(35.5, 2.22) * mm});
            skLineSegment(sketch, "E892", {"start": v(35.5, 2.22) * mm, "end": v(35.28, 1.9) * mm});
            skLineSegment(sketch, "E893", {"start": v(35.28, 1.9) * mm, "end": v(35.08, 1.58) * mm});
            skLineSegment(sketch, "E894", {"start": v(35.08, 1.58) * mm, "end": v(34.9, 1.24) * mm});
            skLineSegment(sketch, "E895", {"start": v(34.9, 1.24) * mm, "end": v(34.74, 0.9) * mm});
            skLineSegment(sketch, "E896", {"start": v(34.74, 0.9) * mm, "end": v(34.58, 0.54) * mm});
            skLineSegment(sketch, "E897", {"start": v(34.58, 0.54) * mm, "end": v(34.45, 0.18) * mm});
            skLineSegment(sketch, "E898", {"start": v(34.45, 0.18) * mm, "end": v(34.34, -0.2) * mm});
            skLineSegment(sketch, "E899", {"start": v(34.34, -0.2) * mm, "end": v(34.25, -0.58) * mm});
            skLineSegment(sketch, "E900", {"start": v(34.25, -0.58) * mm, "end": v(34.18, -0.97) * mm});
            skLineSegment(sketch, "E901", {"start": v(34.18, -0.97) * mm, "end": v(34.13, -1.36) * mm});
            skLineSegment(sketch, "E902", {"start": v(34.13, -1.36) * mm, "end": v(34.1, -1.77) * mm});
            skLineSegment(sketch, "E903", {"start": v(34.1, -1.77) * mm, "end": v(34.09, -2.19) * mm});
            skLineSegment(sketch, "E904", {"start": v(34.09, -2.19) * mm, "end": v(34.1, -2.58) * mm});
            skLineSegment(sketch, "E905", {"start": v(34.1, -2.58) * mm, "end": v(34.13, -2.97) * mm});
            skLineSegment(sketch, "E906", {"start": v(34.13, -2.97) * mm, "end": v(34.18, -3.35) * mm});
            skLineSegment(sketch, "E907", {"start": v(34.18, -3.35) * mm, "end": v(34.25, -3.73) * mm});
            skLineSegment(sketch, "E908", {"start": v(34.25, -3.73) * mm, "end": v(34.34, -4.1) * mm});
            skLineSegment(sketch, "E909", {"start": v(34.34, -4.1) * mm, "end": v(34.44, -4.47) * mm});
            skLineSegment(sketch, "E910", {"start": v(34.44, -4.47) * mm, "end": v(34.57, -4.83) * mm});
            skLineSegment(sketch, "E911", {"start": v(34.57, -4.83) * mm, "end": v(34.72, -5.19) * mm});
            skLineSegment(sketch, "E912", {"start": v(34.72, -5.19) * mm, "end": v(34.88, -5.54) * mm});
            skLineSegment(sketch, "E913", {"start": v(34.88, -5.54) * mm, "end": v(35.07, -5.87) * mm});
            skLineSegment(sketch, "E914", {"start": v(35.07, -5.87) * mm, "end": v(35.26, -6.2) * mm});
            skLineSegment(sketch, "E915", {"start": v(35.26, -6.2) * mm, "end": v(35.48, -6.52) * mm});
            skLineSegment(sketch, "E916", {"start": v(35.48, -6.52) * mm, "end": v(35.7, -6.82) * mm});
            skLineSegment(sketch, "E917", {"start": v(35.7, -6.82) * mm, "end": v(35.95, -7.11) * mm});
            skLineSegment(sketch, "E918", {"start": v(35.95, -7.11) * mm, "end": v(36.2, -7.4) * mm});
            skLineSegment(sketch, "E919", {"start": v(36.2, -7.4) * mm, "end": v(36.48, -7.66) * mm});
            skLineSegment(sketch, "E920", {"start": v(36.48, -7.66) * mm, "end": v(36.76, -7.91) * mm});
            skLineSegment(sketch, "E921", {"start": v(36.76, -7.91) * mm, "end": v(37.06, -8.15) * mm});
            skLineSegment(sketch, "E922", {"start": v(37.06, -8.15) * mm, "end": v(37.37, -8.38) * mm});
            skLineSegment(sketch, "E923", {"start": v(37.37, -8.38) * mm, "end": v(37.7, -8.6) * mm});
            skLineSegment(sketch, "E924", {"start": v(37.7, -8.6) * mm, "end": v(38.04, -8.8) * mm});
            skLineSegment(sketch, "E925", {"start": v(38.04, -8.8) * mm, "end": v(38.39, -8.98) * mm});
            skLineSegment(sketch, "E926", {"start": v(38.39, -8.98) * mm, "end": v(38.75, -9.15) * mm});
            skLineSegment(sketch, "E927", {"start": v(38.75, -9.15) * mm, "end": v(39.13, -9.31) * mm});
            skLineSegment(sketch, "E928", {"start": v(39.13, -9.31) * mm, "end": v(39.52, -9.45) * mm});
            skLineSegment(sketch, "E929", {"start": v(39.52, -9.45) * mm, "end": v(39.91, -9.58) * mm});
            skLineSegment(sketch, "E930", {"start": v(39.91, -9.58) * mm, "end": v(40.32, -9.68) * mm});
            skLineSegment(sketch, "E931", {"start": v(40.32, -9.68) * mm, "end": v(40.73, -9.77) * mm});
            skLineSegment(sketch, "E932", {"start": v(40.73, -9.77) * mm, "end": v(41.15, -9.83) * mm});
            skLineSegment(sketch, "E933", {"start": v(41.15, -9.83) * mm, "end": v(41.58, -9.88) * mm});
            skLineSegment(sketch, "E934", {"start": v(41.58, -9.88) * mm, "end": v(42.01, -9.91) * mm});
            skLineSegment(sketch, "E935", {"start": v(42.01, -9.91) * mm, "end": v(42.45, -9.92) * mm});
            skLineSegment(sketch, "E936", {"start": v(42.45, -9.92) * mm, "end": v(42.9, -9.91) * mm});
            skLineSegment(sketch, "E937", {"start": v(42.9, -9.91) * mm, "end": v(43.34, -9.88) * mm});
            skLineSegment(sketch, "E938", {"start": v(43.34, -9.88) * mm, "end": v(43.77, -9.83) * mm});
            skLineSegment(sketch, "E939", {"start": v(43.77, -9.83) * mm, "end": v(44.2, -9.76) * mm});
            skLineSegment(sketch, "E940", {"start": v(44.2, -9.76) * mm, "end": v(44.61, -9.67) * mm});
            skLineSegment(sketch, "E941", {"start": v(44.61, -9.67) * mm, "end": v(45.02, -9.57) * mm});
            skLineSegment(sketch, "E942", {"start": v(45.02, -9.57) * mm, "end": v(45.42, -9.44) * mm});
            skLineSegment(sketch, "E943", {"start": v(45.42, -9.44) * mm, "end": v(45.81, -9.3) * mm});
            skLineSegment(sketch, "E944", {"start": v(45.81, -9.3) * mm, "end": v(46.2, -9.13) * mm});
            skLineSegment(sketch, "E945", {"start": v(46.2, -9.13) * mm, "end": v(46.56, -8.96) * mm});
            skLineSegment(sketch, "E946", {"start": v(46.56, -8.96) * mm, "end": v(46.92, -8.77) * mm});
            skLineSegment(sketch, "E947", {"start": v(46.92, -8.77) * mm, "end": v(47.26, -8.56) * mm});
            skLineSegment(sketch, "E948", {"start": v(47.26, -8.56) * mm, "end": v(47.6, -8.35) * mm});
            skLineSegment(sketch, "E949", {"start": v(47.6, -8.35) * mm, "end": v(47.9, -8.12) * mm});
            skLineSegment(sketch, "E950", {"start": v(47.9, -8.12) * mm, "end": v(48.2, -7.87) * mm});
            skLineSegment(sketch, "E951", {"start": v(48.2, -7.87) * mm, "end": v(48.5, -7.61) * mm});
            skLineSegment(sketch, "E952", {"start": v(48.5, -7.61) * mm, "end": v(48.76, -7.34) * mm});
            skLineSegment(sketch, "E953", {"start": v(48.76, -7.34) * mm, "end": v(49.02, -7.06) * mm});
            skLineSegment(sketch, "E954", {"start": v(49.02, -7.06) * mm, "end": v(49.26, -6.77) * mm});
            skLineSegment(sketch, "E955", {"start": v(49.26, -6.77) * mm, "end": v(49.5, -6.46) * mm});
            skLineSegment(sketch, "E956", {"start": v(49.5, -6.46) * mm, "end": v(49.7, -6.15) * mm});
            skLineSegment(sketch, "E957", {"start": v(49.7, -6.15) * mm, "end": v(49.9, -5.82) * mm});
            skLineSegment(sketch, "E958", {"start": v(49.9, -5.82) * mm, "end": v(50.09, -5.49) * mm});
            skLineSegment(sketch, "E959", {"start": v(50.09, -5.49) * mm, "end": v(50.25, -5.14) * mm});
            skLineSegment(sketch, "E960", {"start": v(50.25, -5.14) * mm, "end": v(50.4, -4.79) * mm});
            skLineSegment(sketch, "E961", {"start": v(50.4, -4.79) * mm, "end": v(50.53, -4.42) * mm});
            skLineSegment(sketch, "E962", {"start": v(50.53, -4.42) * mm, "end": v(50.64, -4.05) * mm});
            skLineSegment(sketch, "E963", {"start": v(50.64, -4.05) * mm, "end": v(50.73, -3.67) * mm});
            skLineSegment(sketch, "E964", {"start": v(50.73, -3.67) * mm, "end": v(50.8, -3.29) * mm});
            skLineSegment(sketch, "E965", {"start": v(50.8, -3.29) * mm, "end": v(50.85, -2.9) * mm});
            skLineSegment(sketch, "E966", {"start": v(50.85, -2.9) * mm, "end": v(50.88, -2.5) * mm});
            skLineSegment(sketch, "E967", {"start": v(50.88, -2.5) * mm, "end": v(50.9, -2.08) * mm});
            skLineSegment(sketch, "E968", {"start": v(50.9, -2.08) * mm, "end": v(50.88, -1.68) * mm});
            skLineSegment(sketch, "E969", {"start": v(50.88, -1.68) * mm, "end": v(50.85, -1.3) * mm});
            skLineSegment(sketch, "E970", {"start": v(50.85, -1.3) * mm, "end": v(50.8, -0.9) * mm});
            skLineSegment(sketch, "E971", {"start": v(50.8, -0.9) * mm, "end": v(50.74, -0.52) * mm});
            skLineSegment(sketch, "E972", {"start": v(50.74, -0.52) * mm, "end": v(50.65, -0.15) * mm});
            skLineSegment(sketch, "E973", {"start": v(50.65, -0.15) * mm, "end": v(50.54, 0.22) * mm});
            skLineSegment(sketch, "E974", {"start": v(50.54, 0.22) * mm, "end": v(50.42, 0.58) * mm});
            skLineSegment(sketch, "E975", {"start": v(50.42, 0.58) * mm, "end": v(50.27, 0.93) * mm});
            skLineSegment(sketch, "E976", {"start": v(54.1, -12.63) * mm, "end": v(-54.1, -12.63) * mm});
            skLineSegment(sketch, "E977", {"start": v(-54.1, -12.63) * mm, "end": v(-54.1, 12.63) * mm});
            skLineSegment(sketch, "E978", {"start": v(-54.1, 12.63) * mm, "end": v(54.1, 12.63) * mm});
            skLineSegment(sketch, "E979", {"start": v(54.1, 12.63) * mm, "end": v(54.1, -12.63) * mm});
            skSolve(sketch);
        }
        {
            var Q0;
            Q0=makeQuery(id+"F0.imprint","IMPRINT",FACE,{"disambiguationData":[TD([[makeQuery(id+"F0.imprint","IMPRINT",EDGE,{"derivedFrom":sQuery(id+"F0.wireOp",EDGE,"E0")}),1.0]])]});
            var Q1;
            Q1=makeQuery(id+"F0.imprint","IMPRINT",FACE,{"disambiguationData":[TD([[makeQuery(id+"F0.imprint","IMPRINT",EDGE,{"derivedFrom":sQuery(id+"F0.wireOp",EDGE,"E48")}),1.0]])]});
            var Q2;
            Q2=makeQuery(id+"F0.imprint","IMPRINT",FACE,{"disambiguationData":[TD([[makeQuery(id+"F0.imprint","IMPRINT",EDGE,{"derivedFrom":sQuery(id+"F0.wireOp",EDGE,"E304")}),1.0]])]});
            var Q3;
            Q3=makeQuery(id+"F0.imprint","IMPRINT",FACE,{"disambiguationData":[TD([[makeQuery(id+"F0.imprint","IMPRINT",EDGE,{"derivedFrom":sQuery(id+"F0.wireOp",EDGE,"E440")}),1.0]])]});
            var Q4;
            Q4=makeQuery(id+"F0.imprint","IMPRINT",FACE,{"disambiguationData":[TD([[makeQuery(id+"F0.imprint","IMPRINT",EDGE,{"derivedFrom":sQuery(id+"F0.wireOp",EDGE,"E680")}),1.0]])]});
            var Q5;
            Q5=makeQuery(id+"F0.imprint","IMPRINT",FACE,{"disambiguationData":[TD([[makeQuery(id+"F0.imprint","IMPRINT",EDGE,{"derivedFrom":sQuery(id+"F0.wireOp",EDGE,"E736")}),1.0]])]});
            extrude(context, id + "F1", {"entities" : qUnion([Q0, Q1, Q2, Q3, Q4, Q5]), "depth" : 5 * mm, "offsetDistance" : 25 * mm});
        }
        {
            var Q0;
            Q0=makeQuery(id+"F0.imprint","IMPRINT",FACE,{"disambiguationData":[TD([[makeQuery(id+"F0.imprint","IMPRINT",EDGE,{"derivedFrom":sQuery(id+"F0.wireOp",EDGE,"E0")}),-1.0]])]});
            var Q1;
            Q1=makeQuery(id+"F0.imprint","IMPRINT",FACE,{"disambiguationData":[TD([[makeQuery(id+"F0.imprint","IMPRINT",EDGE,{"derivedFrom":sQuery(id+"F0.wireOp",EDGE,"E0")}),1.0]])]});
            var Q2;
            Q2=makeQuery(id+"F0.imprint","IMPRINT",FACE,{"disambiguationData":[TD([[makeQuery(id+"F0.imprint","IMPRINT",EDGE,{"derivedFrom":sQuery(id+"F0.wireOp",EDGE,"E48")}),1.0]])]});
            var Q3;
            Q3=makeQuery(id+"F0.imprint","IMPRINT",FACE,{"disambiguationData":[TD([[makeQuery(id+"F0.imprint","IMPRINT",EDGE,{"derivedFrom":sQuery(id+"F0.wireOp",EDGE,"E48")}),-1.0]])]});
            var Q4;
            Q4=makeQuery(id+"F0.imprint","IMPRINT",FACE,{"disambiguationData":[TD([[makeQuery(id+"F0.imprint","IMPRINT",EDGE,{"derivedFrom":sQuery(id+"F0.wireOp",EDGE,"E304")}),1.0]])]});
            var Q5;
            Q5=makeQuery(id+"F0.imprint","IMPRINT",FACE,{"disambiguationData":[TD([[makeQuery(id+"F0.imprint","IMPRINT",EDGE,{"derivedFrom":sQuery(id+"F0.wireOp",EDGE,"E440")}),-1.0]])]});
            var Q6;
            Q6=makeQuery(id+"F0.imprint","IMPRINT",FACE,{"disambiguationData":[TD([[makeQuery(id+"F0.imprint","IMPRINT",EDGE,{"derivedFrom":sQuery(id+"F0.wireOp",EDGE,"E440")}),1.0]])]});
            var Q7;
            Q7=makeQuery(id+"F0.imprint","IMPRINT",FACE,{"disambiguationData":[TD([[makeQuery(id+"F0.imprint","IMPRINT",EDGE,{"derivedFrom":sQuery(id+"F0.wireOp",EDGE,"E680")}),1.0]])]});
            var Q8;
            Q8=makeQuery(id+"F0.imprint","IMPRINT",FACE,{"disambiguationData":[TD([[makeQuery(id+"F0.imprint","IMPRINT",EDGE,{"derivedFrom":sQuery(id+"F0.wireOp",EDGE,"E736")}),1.0]])]});
            var Q9;
            Q9=makeQuery(id+"F0.imprint","IMPRINT",FACE,{"disambiguationData":[TD([[makeQuery(id+"F0.imprint","IMPRINT",EDGE,{"derivedFrom":sQuery(id+"F0.wireOp",EDGE,"E736")}),-1.0]])]});
            extrude(context, id + "F2", {"entities" : qUnion([Q0, Q1, Q2, Q3, Q4, Q5, Q6, Q7, Q8, Q9]), "oppositeDirection" : true, "depth" : 0.5 * mm, "offsetDistance" : 25 * mm});
        }
    });
